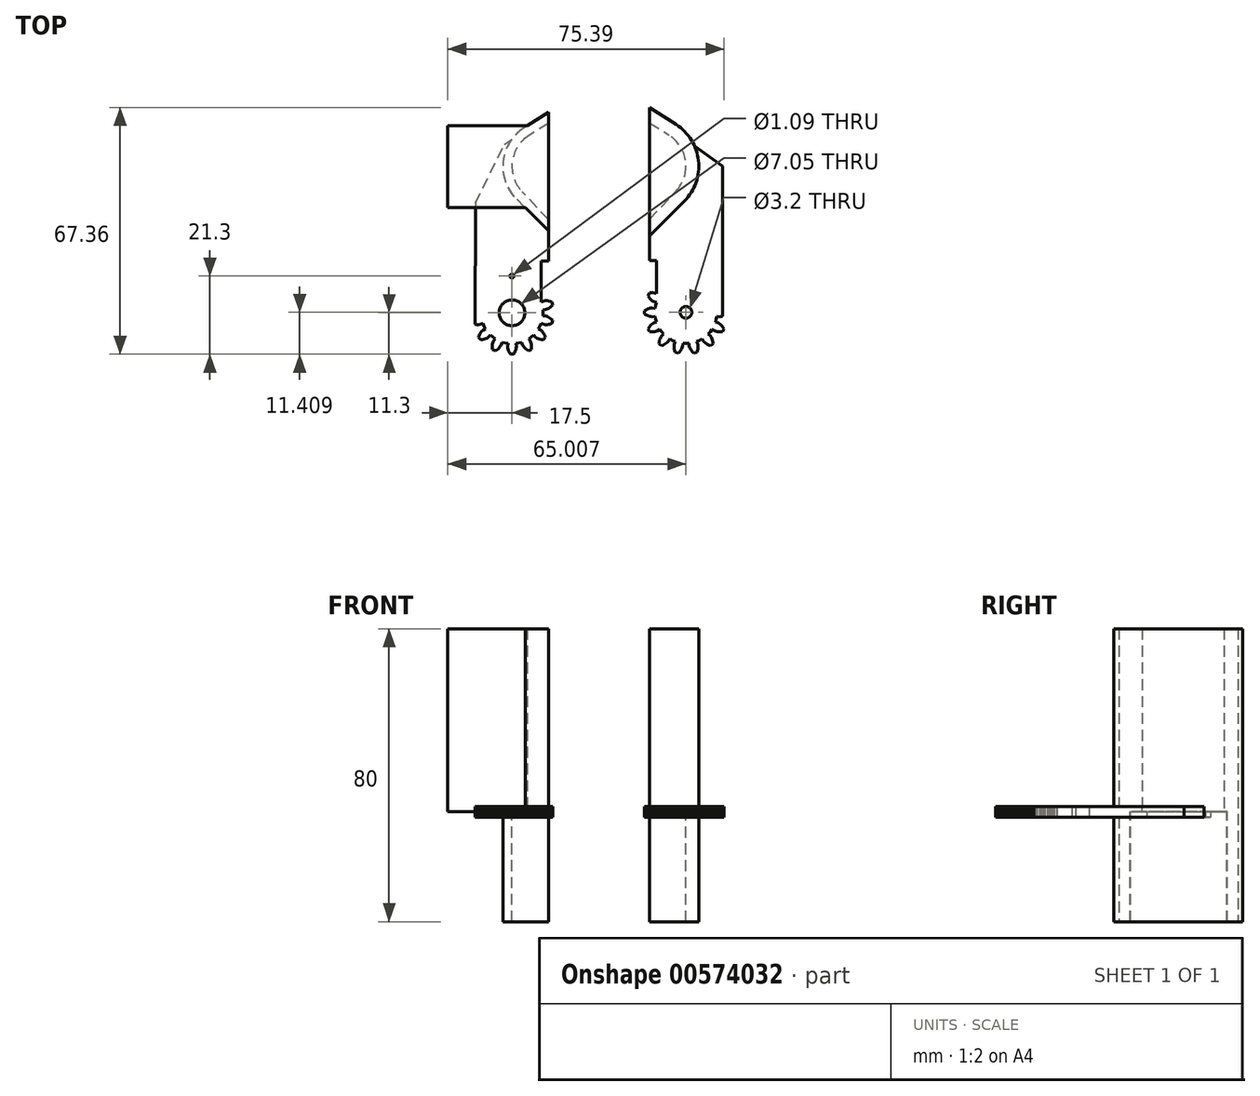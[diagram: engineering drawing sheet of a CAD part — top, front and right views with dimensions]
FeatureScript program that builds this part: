
annotation { "Feature Type Name" : "Feature", "Feature Type Description" : "" }
export const myFeature = defineFeature(function(context is Context, id is Id, definition is map)
    precondition{}
    {
        {
            var Q0;
            Q0=qCreatedBy(makeId("Top.planeOp"),FACE);
            var sketch = newSketch(context, id + "F0", { "sketchPlane" : qUnion([Q0])});
            skLineSegment(sketch, "E0", {"start": v(-11.89, -38.22) * mm, "end": v(-11.08, -38.37) * mm});
            skLineSegment(sketch, "E1", {"start": v(-11.08, -38.37) * mm, "end": v(-11.18, -39.18) * mm});
            skLineSegment(sketch, "E2", {"start": v(-11.18, -39.18) * mm, "end": v(-11.15, -39.59) * mm});
            skLineSegment(sketch, "E3", {"start": v(-11.15, -39.59) * mm, "end": v(-11.05, -40) * mm});
            skLineSegment(sketch, "E4", {"start": v(-11.05, -40) * mm, "end": v(-10.9, -40.42) * mm});
            skLineSegment(sketch, "E5", {"start": v(-10.9, -40.42) * mm, "end": v(-10.7, -40.84) * mm});
            skLineSegment(sketch, "E6", {"start": v(-10.7, -40.84) * mm, "end": v(-10.46, -41.25) * mm});
            skLineSegment(sketch, "E7", {"start": v(-10.46, -41.25) * mm, "end": v(-9.54, -41.25) * mm});
            skLineSegment(sketch, "E8", {"start": v(-9.54, -41.25) * mm, "end": v(-9.3, -40.84) * mm});
            skLineSegment(sketch, "E9", {"start": v(-9.3, -40.84) * mm, "end": v(-9.1, -40.42) * mm});
            skLineSegment(sketch, "E10", {"start": v(-9.1, -40.42) * mm, "end": v(-8.95, -40) * mm});
            skLineSegment(sketch, "E11", {"start": v(-8.95, -40) * mm, "end": v(-8.85, -39.59) * mm});
            skLineSegment(sketch, "E12", {"start": v(-8.85, -39.59) * mm, "end": v(-8.82, -39.18) * mm});
            skLineSegment(sketch, "E13", {"start": v(-8.82, -39.18) * mm, "end": v(-8.92, -38.37) * mm});
            skLineSegment(sketch, "E14", {"start": v(-8.92, -38.37) * mm, "end": v(-8.11, -38.22) * mm});
            skLineSegment(sketch, "E15", {"start": v(-8.11, -38.22) * mm, "end": v(-8.11, -38.22) * mm});
            skLineSegment(sketch, "E16", {"start": v(-8.11, -38.22) * mm, "end": v(-7.32, -38) * mm});
            skLineSegment(sketch, "E17", {"start": v(-7.32, -38) * mm, "end": v(-7.06, -38.78) * mm});
            skLineSegment(sketch, "E18", {"start": v(-7.06, -38.78) * mm, "end": v(-6.86, -39.13) * mm});
            skLineSegment(sketch, "E19", {"start": v(-6.86, -39.13) * mm, "end": v(-6.58, -39.46) * mm});
            skLineSegment(sketch, "E20", {"start": v(-6.58, -39.46) * mm, "end": v(-6.26, -39.77) * mm});
            skLineSegment(sketch, "E21", {"start": v(-6.26, -39.77) * mm, "end": v(-5.9, -40.06) * mm});
            skLineSegment(sketch, "E22", {"start": v(-5.9, -40.06) * mm, "end": v(-5.5, -40.33) * mm});
            skLineSegment(sketch, "E23", {"start": v(-5.5, -40.33) * mm, "end": v(-4.68, -39.94) * mm});
            skLineSegment(sketch, "E24", {"start": v(-4.68, -39.94) * mm, "end": v(-4.65, -39.46) * mm});
            skLineSegment(sketch, "E25", {"start": v(-4.65, -39.46) * mm, "end": v(-4.65, -39) * mm});
            skLineSegment(sketch, "E26", {"start": v(-4.7, -38.55) * mm, "end": v(-4.78, -38.13) * mm});
            skLineSegment(sketch, "E27", {"start": v(-4.78, -38.13) * mm, "end": v(-4.93, -37.75) * mm});
            skLineSegment(sketch, "E28", {"start": v(-4.93, -37.75) * mm, "end": v(-5.38, -37.07) * mm});
            skLineSegment(sketch, "E29", {"start": v(-4.09, -36.04) * mm, "end": v(-3.52, -36.62) * mm});
            skLineSegment(sketch, "E30", {"start": v(-3.18, -36.86) * mm, "end": v(-2.8, -37.04) * mm});
            skLineSegment(sketch, "E31", {"start": v(-2.37, -37.18) * mm, "end": v(-1.92, -37.28) * mm});
            skLineSegment(sketch, "E32", {"start": v(-1.05, -36.2) * mm, "end": v(-1.25, -35.78) * mm});
            skLineSegment(sketch, "E33", {"start": v(-1.25, -35.78) * mm, "end": v(-1.49, -35.4) * mm});
            skLineSegment(sketch, "E34", {"start": v(-2.05, -34.78) * mm, "end": v(-2.75, -34.36) * mm});
            skLineSegment(sketch, "E35", {"start": v(-2.03, -32.87) * mm, "end": v(-1.27, -33.15) * mm});
            skLineSegment(sketch, "E36", {"start": v(-20, -33.15) * mm, "end": v(-19.57, -33.2) * mm});
            skLineSegment(sketch, "E37", {"start": v(-19.57, -33.2) * mm, "end": v(-19.14, -33.22) * mm});
            skLineSegment(sketch, "E38", {"start": v(-19.14, -33.22) * mm, "end": v(-18.73, -33.15) * mm});
            skLineSegment(sketch, "E39", {"start": v(-18.73, -33.15) * mm, "end": v(-17.97, -32.87) * mm});
            skLineSegment(sketch, "E40", {"start": v(-17.97, -32.87) * mm, "end": v(-17.64, -33.63) * mm});
            skLineSegment(sketch, "E41", {"start": v(-17.64, -33.63) * mm, "end": v(-17.65, -33.63) * mm});
            skLineSegment(sketch, "E42", {"start": v(-17.65, -33.63) * mm, "end": v(-17.25, -34.36) * mm});
            skLineSegment(sketch, "E43", {"start": v(-17.25, -34.36) * mm, "end": v(-17.95, -34.78) * mm});
            skLineSegment(sketch, "E44", {"start": v(-17.95, -34.78) * mm, "end": v(-18.25, -35.06) * mm});
            skLineSegment(sketch, "E45", {"start": v(-18.25, -35.06) * mm, "end": v(-18.51, -35.4) * mm});
            skLineSegment(sketch, "E46", {"start": v(-18.51, -35.4) * mm, "end": v(-18.75, -35.78) * mm});
            skLineSegment(sketch, "E47", {"start": v(-18.75, -35.78) * mm, "end": v(-18.95, -36.2) * mm});
            skLineSegment(sketch, "E48", {"start": v(-18.95, -36.2) * mm, "end": v(-19.12, -36.64) * mm});
            skLineSegment(sketch, "E49", {"start": v(-19.12, -36.64) * mm, "end": v(-18.55, -37.36) * mm});
            skLineSegment(sketch, "E50", {"start": v(-18.55, -37.36) * mm, "end": v(-18.08, -37.28) * mm});
            skLineSegment(sketch, "E51", {"start": v(-18.08, -37.28) * mm, "end": v(-17.63, -37.18) * mm});
            skLineSegment(sketch, "E52", {"start": v(-17.63, -37.18) * mm, "end": v(-17.2, -37.04) * mm});
            skLineSegment(sketch, "E53", {"start": v(-17.2, -37.04) * mm, "end": v(-16.82, -36.86) * mm});
            skLineSegment(sketch, "E54", {"start": v(-16.82, -36.86) * mm, "end": v(-16.48, -36.62) * mm});
            skLineSegment(sketch, "E55", {"start": v(-16.48, -36.62) * mm, "end": v(-15.91, -36.04) * mm});
            skLineSegment(sketch, "E56", {"start": v(-15.91, -36.04) * mm, "end": v(-15.3, -36.58) * mm});
            skLineSegment(sketch, "E57", {"start": v(-15.3, -36.58) * mm, "end": v(-15.3, -36.58) * mm});
            skLineSegment(sketch, "E58", {"start": v(-15.3, -36.58) * mm, "end": v(-14.62, -37.07) * mm});
            skLineSegment(sketch, "E59", {"start": v(-14.62, -37.07) * mm, "end": v(-15.07, -37.75) * mm});
            skLineSegment(sketch, "E60", {"start": v(-15.07, -37.75) * mm, "end": v(-15.22, -38.13) * mm});
            skLineSegment(sketch, "E61", {"start": v(-15.22, -38.13) * mm, "end": v(-15.3, -38.55) * mm});
            skLineSegment(sketch, "E62", {"start": v(-15.3, -38.55) * mm, "end": v(-15.35, -39) * mm});
            skLineSegment(sketch, "E63", {"start": v(-15.35, -39) * mm, "end": v(-15.35, -39.46) * mm});
            skLineSegment(sketch, "E64", {"start": v(-15.35, -39.46) * mm, "end": v(-15.32, -39.94) * mm});
            skLineSegment(sketch, "E65", {"start": v(-15.32, -39.94) * mm, "end": v(-14.5, -40.33) * mm});
            skLineSegment(sketch, "E66", {"start": v(-14.5, -40.33) * mm, "end": v(-14.1, -40.06) * mm});
            skLineSegment(sketch, "E67", {"start": v(-14.1, -40.06) * mm, "end": v(-13.74, -39.77) * mm});
            skLineSegment(sketch, "E68", {"start": v(-13.74, -39.77) * mm, "end": v(-13.42, -39.46) * mm});
            skLineSegment(sketch, "E69", {"start": v(-13.42, -39.46) * mm, "end": v(-13.14, -39.13) * mm});
            skLineSegment(sketch, "E70", {"start": v(-13.14, -39.13) * mm, "end": v(-12.94, -38.78) * mm});
            skLineSegment(sketch, "E71", {"start": v(-12.94, -38.78) * mm, "end": v(-12.68, -38) * mm});
            skLineSegment(sketch, "E72", {"start": v(-12.68, -38) * mm, "end": v(-11.89, -38.22) * mm});
            skLineSegment(sketch, "E73", {"start": v(-11.89, -38.22) * mm, "end": v(-11.89, -38.22) * mm});
            skLineSegment(sketch, "E74", {"start": v(-2, -27.02) * mm, "end": v(-2, -15.8) * mm});
            skLineSegment(sketch, "E75", {"start": v(-4.65, -39) * mm, "end": v(-4.7, -38.55) * mm});
            skLineSegment(sketch, "E76", {"start": v(-5.38, -37.07) * mm, "end": v(-4.7, -36.58) * mm});
            skLineSegment(sketch, "E77", {"start": v(-4.7, -36.58) * mm, "end": v(-4.7, -36.58) * mm});
            skLineSegment(sketch, "E78", {"start": v(-4.7, -36.58) * mm, "end": v(-4.09, -36.04) * mm});
            skLineSegment(sketch, "E79", {"start": v(-3.52, -36.62) * mm, "end": v(-3.18, -36.86) * mm});
            skLineSegment(sketch, "E80", {"start": v(-2.8, -37.04) * mm, "end": v(-2.37, -37.18) * mm});
            skLineSegment(sketch, "E81", {"start": v(-1.92, -37.28) * mm, "end": v(-1.45, -37.36) * mm});
            skLineSegment(sketch, "E82", {"start": v(-1.45, -37.36) * mm, "end": v(-0.88, -36.64) * mm});
            skLineSegment(sketch, "E83", {"start": v(-0.88, -36.64) * mm, "end": v(-1.05, -36.2) * mm});
            skLineSegment(sketch, "E84", {"start": v(-1.49, -35.4) * mm, "end": v(-1.75, -35.06) * mm});
            skLineSegment(sketch, "E85", {"start": v(-1.75, -35.06) * mm, "end": v(-2.05, -34.78) * mm});
            skLineSegment(sketch, "E86", {"start": v(-2.75, -34.36) * mm, "end": v(-2.35, -33.63) * mm});
            skLineSegment(sketch, "E87", {"start": v(-2.35, -33.63) * mm, "end": v(-2.36, -33.63) * mm});
            skLineSegment(sketch, "E88", {"start": v(-2.36, -33.63) * mm, "end": v(-2.03, -32.87) * mm});
            skLineSegment(sketch, "E89", {"start": v(-1.27, -33.15) * mm, "end": v(-0.86, -33.22) * mm});
            skLineSegment(sketch, "E90", {"start": v(-0.86, -33.22) * mm, "end": v(-0.43, -33.2) * mm});
            skLineSegment(sketch, "E91", {"start": v(-0.43, -33.2) * mm, "end": v(0, -33.15) * mm});
            skLineSegment(sketch, "E92", {"start": v(0, -33.15) * mm, "end": v(0.46, -33.05) * mm});
            skLineSegment(sketch, "E93", {"start": v(0.46, -33.05) * mm, "end": v(0.92, -32.91) * mm});
            skLineSegment(sketch, "E94", {"start": v(0.92, -32.91) * mm, "end": v(1.12, -32.02) * mm});
            skLineSegment(sketch, "E95", {"start": v(1.12, -32.02) * mm, "end": v(0.77, -31.7) * mm});
            skLineSegment(sketch, "E96", {"start": v(0.77, -31.7) * mm, "end": v(0.4, -31.4) * mm});
            skLineSegment(sketch, "E97", {"start": v(0.4, -31.4) * mm, "end": v(0.03, -31.16) * mm});
            skLineSegment(sketch, "E98", {"start": v(0.03, -31.16) * mm, "end": v(-0.35, -30.97) * mm});
            skLineSegment(sketch, "E99", {"start": v(-0.35, -30.97) * mm, "end": v(-0.74, -30.85) * mm});
            skLineSegment(sketch, "E100", {"start": v(-0.74, -30.85) * mm, "end": v(-1.55, -30.77) * mm});
            skLineSegment(sketch, "E101", {"start": v(-1.55, -30.77) * mm, "end": v(-1.51, -29.95) * mm});
            skLineSegment(sketch, "E102", {"start": v(-1.51, -29.95) * mm, "end": v(-1.51, -29.95) * mm});
            skLineSegment(sketch, "E103", {"start": v(-1.51, -29.95) * mm, "end": v(-1.55, -29.13) * mm});
            skLineSegment(sketch, "E104", {"start": v(-1.55, -29.13) * mm, "end": v(-0.74, -29.05) * mm});
            skLineSegment(sketch, "E105", {"start": v(-0.74, -29.05) * mm, "end": v(-0.35, -28.93) * mm});
            skLineSegment(sketch, "E106", {"start": v(-0.35, -28.93) * mm, "end": v(0.03, -28.74) * mm});
            skLineSegment(sketch, "E107", {"start": v(0.03, -28.74) * mm, "end": v(0.4, -28.5) * mm});
            skLineSegment(sketch, "E108", {"start": v(0.4, -28.5) * mm, "end": v(0.77, -28.2) * mm});
            skLineSegment(sketch, "E109", {"start": v(0.77, -28.2) * mm, "end": v(1.12, -27.88) * mm});
            skLineSegment(sketch, "E110", {"start": v(1.12, -27.88) * mm, "end": v(0.92, -26.99) * mm});
            skLineSegment(sketch, "E111", {"start": v(0.92, -26.99) * mm, "end": v(0.46, -26.85) * mm});
            skLineSegment(sketch, "E112", {"start": v(0.46, -26.85) * mm, "end": v(0, -26.75) * mm});
            skLineSegment(sketch, "E113", {"start": v(0, -26.75) * mm, "end": v(-0.43, -26.69) * mm});
            skLineSegment(sketch, "E114", {"start": v(-0.43, -26.69) * mm, "end": v(-0.86, -26.68) * mm});
            skLineSegment(sketch, "E115", {"start": v(-0.86, -26.68) * mm, "end": v(-1.27, -26.75) * mm});
            skLineSegment(sketch, "E116", {"start": v(-1.27, -26.75) * mm, "end": v(-2, -27.02) * mm});
            skLineSegment(sketch, "E117", {"start": v(45.78, -31.73) * mm, "end": v(45.92, -30.92) * mm});
            skLineSegment(sketch, "E118", {"start": v(45.92, -30.92) * mm, "end": v(46.73, -31.02) * mm});
            skLineSegment(sketch, "E119", {"start": v(46.73, -31.02) * mm, "end": v(47.14, -31) * mm});
            skLineSegment(sketch, "E120", {"start": v(47.14, -31) * mm, "end": v(47.5, -30.9) * mm});
            skLineSegment(sketch, "E121", {"start": v(27.87, -31) * mm, "end": v(28.28, -31.02) * mm});
            skLineSegment(sketch, "E122", {"start": v(29.1, -30.92) * mm, "end": v(29.23, -31.73) * mm});
            skLineSegment(sketch, "E123", {"start": v(28.68, -32.78) * mm, "end": v(28.33, -32.99) * mm});
            skLineSegment(sketch, "E124", {"start": v(27.68, -33.58) * mm, "end": v(27.4, -33.94) * mm});
            skLineSegment(sketch, "E125", {"start": v(28.46, -35.2) * mm, "end": v(28.9, -35.15) * mm});
            skLineSegment(sketch, "E126", {"start": v(28.9, -35.15) * mm, "end": v(29.32, -35.06) * mm});
            skLineSegment(sketch, "E127", {"start": v(29.32, -35.06) * mm, "end": v(29.7, -34.9) * mm});
            skLineSegment(sketch, "E128", {"start": v(29.7, -34.9) * mm, "end": v(30.4, -34.46) * mm});
            skLineSegment(sketch, "E129", {"start": v(30.4, -34.46) * mm, "end": v(30.87, -35.13) * mm});
            skLineSegment(sketch, "E130", {"start": v(30.87, -35.13) * mm, "end": v(30.87, -35.13) * mm});
            skLineSegment(sketch, "E131", {"start": v(31.42, -35.75) * mm, "end": v(30.83, -36.32) * mm});
            skLineSegment(sketch, "E132", {"start": v(30.17, -37.92) * mm, "end": v(30.1, -38.4) * mm});
            skLineSegment(sketch, "E133", {"start": v(30.1, -38.4) * mm, "end": v(30.82, -38.96) * mm});
            skLineSegment(sketch, "E134", {"start": v(30.82, -38.96) * mm, "end": v(31.26, -38.8) * mm});
            skLineSegment(sketch, "E135", {"start": v(31.68, -38.59) * mm, "end": v(32.06, -38.35) * mm});
            skLineSegment(sketch, "E136", {"start": v(32.06, -38.35) * mm, "end": v(32.4, -38.1) * mm});
            skLineSegment(sketch, "E137", {"start": v(32.68, -37.8) * mm, "end": v(33.1, -37.1) * mm});
            skLineSegment(sketch, "E138", {"start": v(33.1, -37.1) * mm, "end": v(33.83, -37.49) * mm});
            skLineSegment(sketch, "E139", {"start": v(33.83, -37.49) * mm, "end": v(33.83, -37.49) * mm});
            skLineSegment(sketch, "E140", {"start": v(34.59, -37.8) * mm, "end": v(34.3, -38.58) * mm});
            skLineSegment(sketch, "E141", {"start": v(34.4, -40.3) * mm, "end": v(34.55, -40.76) * mm});
            skLineSegment(sketch, "E142", {"start": v(35.44, -40.96) * mm, "end": v(35.76, -40.61) * mm});
            skLineSegment(sketch, "E143", {"start": v(36.05, -40.25) * mm, "end": v(36.3, -39.88) * mm});
            skLineSegment(sketch, "E144", {"start": v(36.68, -38.29) * mm, "end": v(37.5, -38.33) * mm});
            skLineSegment(sketch, "E145", {"start": v(37.5, -38.33) * mm, "end": v(37.5, -38.33) * mm});
            skLineSegment(sketch, "E146", {"start": v(37.5, -38.33) * mm, "end": v(38.33, -38.29) * mm});
            skLineSegment(sketch, "E147", {"start": v(38.33, -38.29) * mm, "end": v(38.41, -39.1) * mm});
            skLineSegment(sketch, "E148", {"start": v(38.41, -39.1) * mm, "end": v(38.53, -39.5) * mm});
            skLineSegment(sketch, "E149", {"start": v(38.53, -39.5) * mm, "end": v(38.72, -39.88) * mm});
            skLineSegment(sketch, "E150", {"start": v(38.72, -39.88) * mm, "end": v(38.96, -40.25) * mm});
            skLineSegment(sketch, "E151", {"start": v(38.96, -40.25) * mm, "end": v(39.25, -40.61) * mm});
            skLineSegment(sketch, "E152", {"start": v(39.25, -40.61) * mm, "end": v(39.58, -40.96) * mm});
            skLineSegment(sketch, "E153", {"start": v(39.58, -40.96) * mm, "end": v(40.47, -40.76) * mm});
            skLineSegment(sketch, "E154", {"start": v(40.47, -40.76) * mm, "end": v(40.61, -40.3) * mm});
            skLineSegment(sketch, "E155", {"start": v(40.61, -40.3) * mm, "end": v(40.71, -39.85) * mm});
            skLineSegment(sketch, "E156", {"start": v(40.71, -39.85) * mm, "end": v(40.77, -39.4) * mm});
            skLineSegment(sketch, "E157", {"start": v(40.77, -39.4) * mm, "end": v(40.77, -38.98) * mm});
            skLineSegment(sketch, "E158", {"start": v(40.77, -38.98) * mm, "end": v(40.7, -38.58) * mm});
            skLineSegment(sketch, "E159", {"start": v(40.7, -38.58) * mm, "end": v(40.43, -37.8) * mm});
            skLineSegment(sketch, "E160", {"start": v(40.43, -37.8) * mm, "end": v(41.19, -37.49) * mm});
            skLineSegment(sketch, "E161", {"start": v(41.19, -37.49) * mm, "end": v(41.19, -37.49) * mm});
            skLineSegment(sketch, "E162", {"start": v(41.19, -37.49) * mm, "end": v(41.91, -37.1) * mm});
            skLineSegment(sketch, "E163", {"start": v(41.91, -37.1) * mm, "end": v(42.34, -37.8) * mm});
            skLineSegment(sketch, "E164", {"start": v(42.34, -37.8) * mm, "end": v(42.62, -38.1) * mm});
            skLineSegment(sketch, "E165", {"start": v(42.62, -38.1) * mm, "end": v(42.95, -38.35) * mm});
            skLineSegment(sketch, "E166", {"start": v(42.95, -38.35) * mm, "end": v(43.33, -38.59) * mm});
            skLineSegment(sketch, "E167", {"start": v(43.33, -38.59) * mm, "end": v(43.75, -38.8) * mm});
            skLineSegment(sketch, "E168", {"start": v(43.75, -38.8) * mm, "end": v(44.2, -38.96) * mm});
            skLineSegment(sketch, "E169", {"start": v(44.2, -38.96) * mm, "end": v(44.91, -38.4) * mm});
            skLineSegment(sketch, "E170", {"start": v(44.91, -38.4) * mm, "end": v(44.84, -37.92) * mm});
            skLineSegment(sketch, "E171", {"start": v(44.84, -37.92) * mm, "end": v(44.74, -37.47) * mm});
            skLineSegment(sketch, "E172", {"start": v(44.74, -37.47) * mm, "end": v(44.6, -37.05) * mm});
            skLineSegment(sketch, "E173", {"start": v(44.6, -37.05) * mm, "end": v(44.41, -36.66) * mm});
            skLineSegment(sketch, "E174", {"start": v(44.41, -36.66) * mm, "end": v(44.18, -36.32) * mm});
            skLineSegment(sketch, "E175", {"start": v(44.18, -36.32) * mm, "end": v(43.6, -35.75) * mm});
            skLineSegment(sketch, "E176", {"start": v(43.6, -35.75) * mm, "end": v(44.14, -35.13) * mm});
            skLineSegment(sketch, "E177", {"start": v(44.14, -35.13) * mm, "end": v(44.14, -35.13) * mm});
            skLineSegment(sketch, "E178", {"start": v(44.14, -35.13) * mm, "end": v(44.62, -34.46) * mm});
            skLineSegment(sketch, "E179", {"start": v(44.62, -34.46) * mm, "end": v(45.3, -34.9) * mm});
            skLineSegment(sketch, "E180", {"start": v(45.3, -34.9) * mm, "end": v(45.69, -35.06) * mm});
            skLineSegment(sketch, "E181", {"start": v(45.69, -35.06) * mm, "end": v(46.1, -35.15) * mm});
            skLineSegment(sketch, "E182", {"start": v(46.1, -35.15) * mm, "end": v(46.55, -35.2) * mm});
            skLineSegment(sketch, "E183", {"start": v(46.55, -35.2) * mm, "end": v(47.01, -35.2) * mm});
            skLineSegment(sketch, "E184", {"start": v(47.01, -35.2) * mm, "end": v(47.5, -35.16) * mm});
            skLineSegment(sketch, "E185", {"start": v(47.5, -35.16) * mm, "end": v(47.9, -34.33) * mm});
            skLineSegment(sketch, "E186", {"start": v(47.9, -34.33) * mm, "end": v(47.62, -33.94) * mm});
            skLineSegment(sketch, "E187", {"start": v(47.62, -33.94) * mm, "end": v(47.33, -33.58) * mm});
            skLineSegment(sketch, "E188", {"start": v(47.33, -33.58) * mm, "end": v(47.02, -33.26) * mm});
            skLineSegment(sketch, "E189", {"start": v(47.02, -33.26) * mm, "end": v(46.69, -32.99) * mm});
            skLineSegment(sketch, "E190", {"start": v(46.69, -32.99) * mm, "end": v(46.33, -32.78) * mm});
            skLineSegment(sketch, "E191", {"start": v(46.33, -32.78) * mm, "end": v(45.56, -32.52) * mm});
            skLineSegment(sketch, "E192", {"start": v(45.56, -32.52) * mm, "end": v(45.78, -31.73) * mm});
            skLineSegment(sketch, "E193", {"start": v(45.78, -31.73) * mm, "end": v(45.78, -31.73) * mm});
            skLineSegment(sketch, "E194", {"start": v(29.5, -24.7) * mm, "end": v(29.5, -15.7) * mm});
            skLineSegment(sketch, "E195", {"start": v(47.5, -30.9) * mm, "end": v(47.5, 10.1) * mm});
            skLineSegment(sketch, "E196", {"start": v(29.5, -24.7) * mm, "end": v(29.32, -24.62) * mm});
            skLineSegment(sketch, "E197", {"start": v(29.32, -24.62) * mm, "end": v(28.9, -24.53) * mm});
            skLineSegment(sketch, "E198", {"start": v(28.9, -24.53) * mm, "end": v(28.46, -24.5) * mm});
            skLineSegment(sketch, "E199", {"start": v(28.46, -24.5) * mm, "end": v(28, -24.49) * mm});
            skLineSegment(sketch, "E200", {"start": v(28, -24.49) * mm, "end": v(27.52, -24.53) * mm});
            skLineSegment(sketch, "E201", {"start": v(27.52, -24.53) * mm, "end": v(27.12, -25.35) * mm});
            skLineSegment(sketch, "E202", {"start": v(27.12, -25.35) * mm, "end": v(27.4, -25.75) * mm});
            skLineSegment(sketch, "E203", {"start": v(27.4, -25.75) * mm, "end": v(27.68, -26.1) * mm});
            skLineSegment(sketch, "E204", {"start": v(27.68, -26.1) * mm, "end": v(28, -26.43) * mm});
            skLineSegment(sketch, "E205", {"start": v(28, -26.43) * mm, "end": v(28.33, -26.7) * mm});
            skLineSegment(sketch, "E206", {"start": v(28.33, -26.7) * mm, "end": v(28.68, -26.9) * mm});
            skLineSegment(sketch, "E207", {"start": v(28.68, -26.9) * mm, "end": v(29.46, -27.16) * mm});
            skLineSegment(sketch, "E208", {"start": v(29.46, -27.16) * mm, "end": v(29.23, -27.95) * mm});
            skLineSegment(sketch, "E209", {"start": v(29.23, -27.95) * mm, "end": v(29.23, -27.95) * mm});
            skLineSegment(sketch, "E210", {"start": v(29.23, -27.95) * mm, "end": v(29.1, -28.77) * mm});
            skLineSegment(sketch, "E211", {"start": v(29.1, -28.77) * mm, "end": v(28.28, -28.66) * mm});
            skLineSegment(sketch, "E212", {"start": v(28.28, -28.66) * mm, "end": v(27.87, -28.7) * mm});
            skLineSegment(sketch, "E213", {"start": v(27.87, -28.7) * mm, "end": v(27.45, -28.8) * mm});
            skLineSegment(sketch, "E214", {"start": v(27.45, -28.8) * mm, "end": v(27.04, -28.94) * mm});
            skLineSegment(sketch, "E215", {"start": v(27.04, -28.94) * mm, "end": v(26.62, -29.14) * mm});
            skLineSegment(sketch, "E216", {"start": v(26.62, -29.14) * mm, "end": v(26.2, -29.38) * mm});
            skLineSegment(sketch, "E217", {"start": v(26.2, -30.3) * mm, "end": v(26.62, -30.54) * mm});
            skLineSegment(sketch, "E218", {"start": v(26.62, -30.54) * mm, "end": v(27.04, -30.74) * mm});
            skLineSegment(sketch, "E219", {"start": v(27.04, -30.74) * mm, "end": v(27.45, -30.9) * mm});
            skLineSegment(sketch, "E220", {"start": v(27.45, -30.9) * mm, "end": v(27.87, -31) * mm});
            skLineSegment(sketch, "E221", {"start": v(28.28, -31.02) * mm, "end": v(29.1, -30.92) * mm});
            skLineSegment(sketch, "E222", {"start": v(29.23, -31.73) * mm, "end": v(29.23, -31.73) * mm});
            skLineSegment(sketch, "E223", {"start": v(29.23, -31.73) * mm, "end": v(29.46, -32.52) * mm});
            skLineSegment(sketch, "E224", {"start": v(29.46, -32.52) * mm, "end": v(28.68, -32.78) * mm});
            skLineSegment(sketch, "E225", {"start": v(28.33, -32.99) * mm, "end": v(28, -33.26) * mm});
            skLineSegment(sketch, "E226", {"start": v(28, -33.26) * mm, "end": v(27.68, -33.58) * mm});
            skLineSegment(sketch, "E227", {"start": v(27.4, -33.94) * mm, "end": v(27.12, -34.33) * mm});
            skLineSegment(sketch, "E228", {"start": v(27.12, -34.33) * mm, "end": v(27.52, -35.16) * mm});
            skLineSegment(sketch, "E229", {"start": v(27.52, -35.16) * mm, "end": v(28, -35.2) * mm});
            skLineSegment(sketch, "E230", {"start": v(28, -35.2) * mm, "end": v(28.46, -35.2) * mm});
            skLineSegment(sketch, "E231", {"start": v(30.87, -35.13) * mm, "end": v(31.42, -35.75) * mm});
            skLineSegment(sketch, "E232", {"start": v(30.83, -36.32) * mm, "end": v(30.6, -36.66) * mm});
            skLineSegment(sketch, "E233", {"start": v(30.6, -36.66) * mm, "end": v(30.42, -37.05) * mm});
            skLineSegment(sketch, "E234", {"start": v(30.42, -37.05) * mm, "end": v(30.28, -37.47) * mm});
            skLineSegment(sketch, "E235", {"start": v(30.28, -37.47) * mm, "end": v(30.17, -37.92) * mm});
            skLineSegment(sketch, "E236", {"start": v(31.26, -38.8) * mm, "end": v(31.68, -38.59) * mm});
            skLineSegment(sketch, "E237", {"start": v(32.4, -38.1) * mm, "end": v(32.68, -37.8) * mm});
            skLineSegment(sketch, "E238", {"start": v(33.83, -37.49) * mm, "end": v(34.59, -37.8) * mm});
            skLineSegment(sketch, "E239", {"start": v(34.3, -38.58) * mm, "end": v(34.24, -38.98) * mm});
            skLineSegment(sketch, "E240", {"start": v(34.24, -38.98) * mm, "end": v(34.25, -39.4) * mm});
            skLineSegment(sketch, "E241", {"start": v(34.25, -39.4) * mm, "end": v(34.3, -39.85) * mm});
            skLineSegment(sketch, "E242", {"start": v(34.3, -39.85) * mm, "end": v(34.4, -40.3) * mm});
            skLineSegment(sketch, "E243", {"start": v(34.55, -40.76) * mm, "end": v(35.44, -40.96) * mm});
            skLineSegment(sketch, "E244", {"start": v(35.76, -40.61) * mm, "end": v(36.05, -40.25) * mm});
            skLineSegment(sketch, "E245", {"start": v(36.3, -39.88) * mm, "end": v(36.48, -39.5) * mm});
            skLineSegment(sketch, "E246", {"start": v(36.48, -39.5) * mm, "end": v(36.6, -39.1) * mm});
            skLineSegment(sketch, "E247", {"start": v(36.6, -39.1) * mm, "end": v(36.68, -38.29) * mm});
            skLineSegment(sketch, "E248", {"start": v(26.2, -29.38) * mm, "end": v(26.2, -30.3) * mm});
            skCircle(sketch, "E249", {"center": v(37.5, -29.84) * mm, "radius": 1.6 * mm});
            skCircle(sketch, "E250", {"center": v(-10, -29.95) * mm, "radius": 3.52 * mm});
            skCircle(sketch, "E251", {"center": v(-10, -19.95) * mm, "radius": 0.55 * mm});
            skLineSegment(sketch, "E252", {"start": v(97.08, -42.45) * mm, "end": v(97.9, -42.59) * mm});
            skLineSegment(sketch, "E253", {"start": v(97.9, -42.59) * mm, "end": v(97.8, -43.4) * mm});
            skLineSegment(sketch, "E254", {"start": v(97.8, -43.4) * mm, "end": v(97.82, -43.8) * mm});
            skLineSegment(sketch, "E255", {"start": v(97.82, -43.8) * mm, "end": v(97.92, -44.23) * mm});
            skLineSegment(sketch, "E256", {"start": v(97.92, -44.23) * mm, "end": v(98.07, -44.64) * mm});
            skLineSegment(sketch, "E257", {"start": v(98.07, -44.64) * mm, "end": v(98.27, -45.06) * mm});
            skLineSegment(sketch, "E258", {"start": v(98.27, -45.06) * mm, "end": v(98.51, -45.48) * mm});
            skLineSegment(sketch, "E259", {"start": v(98.51, -45.48) * mm, "end": v(99.43, -45.48) * mm});
            skLineSegment(sketch, "E260", {"start": v(99.43, -45.48) * mm, "end": v(99.67, -45.06) * mm});
            skLineSegment(sketch, "E261", {"start": v(99.67, -45.06) * mm, "end": v(99.87, -44.64) * mm});
            skLineSegment(sketch, "E262", {"start": v(99.87, -44.64) * mm, "end": v(100.02, -44.23) * mm});
            skLineSegment(sketch, "E263", {"start": v(100.02, -44.23) * mm, "end": v(100.12, -43.8) * mm});
            skLineSegment(sketch, "E264", {"start": v(100.12, -43.8) * mm, "end": v(100.15, -43.4) * mm});
            skLineSegment(sketch, "E265", {"start": v(100.15, -43.4) * mm, "end": v(100.05, -42.59) * mm});
            skLineSegment(sketch, "E266", {"start": v(100.05, -42.59) * mm, "end": v(100.86, -42.45) * mm});
            skLineSegment(sketch, "E267", {"start": v(100.86, -42.45) * mm, "end": v(100.86, -42.45) * mm});
            skLineSegment(sketch, "E268", {"start": v(100.86, -42.45) * mm, "end": v(101.65, -42.22) * mm});
            skLineSegment(sketch, "E269", {"start": v(101.65, -42.22) * mm, "end": v(101.91, -43) * mm});
            skLineSegment(sketch, "E270", {"start": v(101.91, -43) * mm, "end": v(102.12, -43.35) * mm});
            skLineSegment(sketch, "E271", {"start": v(102.12, -43.35) * mm, "end": v(102.39, -43.68) * mm});
            skLineSegment(sketch, "E272", {"start": v(102.39, -43.68) * mm, "end": v(102.7, -44) * mm});
            skLineSegment(sketch, "E273", {"start": v(102.7, -44) * mm, "end": v(103.07, -44.29) * mm});
            skLineSegment(sketch, "E274", {"start": v(103.07, -44.29) * mm, "end": v(103.46, -44.56) * mm});
            skLineSegment(sketch, "E275", {"start": v(103.46, -44.56) * mm, "end": v(104.29, -44.16) * mm});
            skLineSegment(sketch, "E276", {"start": v(104.29, -44.16) * mm, "end": v(104.32, -43.68) * mm});
            skLineSegment(sketch, "E277", {"start": v(104.32, -43.68) * mm, "end": v(104.32, -43.22) * mm});
            skLineSegment(sketch, "E278", {"start": v(104.28, -42.77) * mm, "end": v(104.19, -42.36) * mm});
            skLineSegment(sketch, "E279", {"start": v(104.19, -42.36) * mm, "end": v(104.04, -41.97) * mm});
            skLineSegment(sketch, "E280", {"start": v(104.04, -41.97) * mm, "end": v(103.6, -41.29) * mm});
            skLineSegment(sketch, "E281", {"start": v(104.88, -40.26) * mm, "end": v(105.45, -40.85) * mm});
            skLineSegment(sketch, "E282", {"start": v(105.79, -41.08) * mm, "end": v(106.18, -41.26) * mm});
            skLineSegment(sketch, "E283", {"start": v(106.6, -41.4) * mm, "end": v(107.05, -41.5) * mm});
            skLineSegment(sketch, "E284", {"start": v(107.92, -40.42) * mm, "end": v(107.72, -40) * mm});
            skLineSegment(sketch, "E285", {"start": v(107.72, -40) * mm, "end": v(107.48, -39.62) * mm});
            skLineSegment(sketch, "E286", {"start": v(106.92, -39) * mm, "end": v(106.22, -38.58) * mm});
            skLineSegment(sketch, "E287", {"start": v(106.94, -37.1) * mm, "end": v(107.7, -37.38) * mm});
            skLineSegment(sketch, "E288", {"start": v(88.96, -37.38) * mm, "end": v(89.4, -37.43) * mm});
            skLineSegment(sketch, "E289", {"start": v(89.4, -37.43) * mm, "end": v(89.83, -37.44) * mm});
            skLineSegment(sketch, "E290", {"start": v(89.83, -37.44) * mm, "end": v(90.24, -37.38) * mm});
            skLineSegment(sketch, "E291", {"start": v(90.24, -37.38) * mm, "end": v(91, -37.1) * mm});
            skLineSegment(sketch, "E292", {"start": v(91, -37.1) * mm, "end": v(91.33, -37.85) * mm});
            skLineSegment(sketch, "E293", {"start": v(91.33, -37.85) * mm, "end": v(91.33, -37.85) * mm});
            skLineSegment(sketch, "E294", {"start": v(91.33, -37.85) * mm, "end": v(91.72, -38.58) * mm});
            skLineSegment(sketch, "E295", {"start": v(91.72, -38.58) * mm, "end": v(91.02, -39) * mm});
            skLineSegment(sketch, "E296", {"start": v(91.02, -39) * mm, "end": v(90.72, -39.28) * mm});
            skLineSegment(sketch, "E297", {"start": v(90.72, -39.28) * mm, "end": v(90.46, -39.62) * mm});
            skLineSegment(sketch, "E298", {"start": v(90.46, -39.62) * mm, "end": v(90.23, -40) * mm});
            skLineSegment(sketch, "E299", {"start": v(90.23, -40) * mm, "end": v(90.02, -40.42) * mm});
            skLineSegment(sketch, "E300", {"start": v(90.02, -40.42) * mm, "end": v(89.85, -40.86) * mm});
            skLineSegment(sketch, "E301", {"start": v(89.85, -40.86) * mm, "end": v(90.42, -41.58) * mm});
            skLineSegment(sketch, "E302", {"start": v(90.42, -41.58) * mm, "end": v(90.9, -41.5) * mm});
            skLineSegment(sketch, "E303", {"start": v(90.9, -41.5) * mm, "end": v(91.34, -41.4) * mm});
            skLineSegment(sketch, "E304", {"start": v(91.34, -41.4) * mm, "end": v(91.77, -41.26) * mm});
            skLineSegment(sketch, "E305", {"start": v(91.77, -41.26) * mm, "end": v(92.15, -41.08) * mm});
            skLineSegment(sketch, "E306", {"start": v(92.15, -41.08) * mm, "end": v(92.5, -40.85) * mm});
            skLineSegment(sketch, "E307", {"start": v(92.5, -40.85) * mm, "end": v(93.06, -40.26) * mm});
            skLineSegment(sketch, "E308", {"start": v(93.06, -40.26) * mm, "end": v(93.68, -40.8) * mm});
            skLineSegment(sketch, "E309", {"start": v(93.68, -40.8) * mm, "end": v(93.68, -40.8) * mm});
            skLineSegment(sketch, "E310", {"start": v(93.68, -40.8) * mm, "end": v(94.35, -41.29) * mm});
            skLineSegment(sketch, "E311", {"start": v(94.35, -41.29) * mm, "end": v(93.9, -41.97) * mm});
            skLineSegment(sketch, "E312", {"start": v(93.9, -41.97) * mm, "end": v(93.75, -42.36) * mm});
            skLineSegment(sketch, "E313", {"start": v(93.75, -42.36) * mm, "end": v(93.66, -42.77) * mm});
            skLineSegment(sketch, "E314", {"start": v(93.66, -42.77) * mm, "end": v(93.62, -43.22) * mm});
            skLineSegment(sketch, "E315", {"start": v(93.62, -43.22) * mm, "end": v(93.62, -43.68) * mm});
            skLineSegment(sketch, "E316", {"start": v(93.62, -43.68) * mm, "end": v(93.65, -44.16) * mm});
            skLineSegment(sketch, "E317", {"start": v(93.65, -44.16) * mm, "end": v(94.48, -44.56) * mm});
            skLineSegment(sketch, "E318", {"start": v(94.48, -44.56) * mm, "end": v(94.87, -44.29) * mm});
            skLineSegment(sketch, "E319", {"start": v(94.87, -44.29) * mm, "end": v(95.24, -44) * mm});
            skLineSegment(sketch, "E320", {"start": v(95.24, -44) * mm, "end": v(95.55, -43.68) * mm});
            skLineSegment(sketch, "E321", {"start": v(95.55, -43.68) * mm, "end": v(95.83, -43.35) * mm});
            skLineSegment(sketch, "E322", {"start": v(95.83, -43.35) * mm, "end": v(96.03, -43) * mm});
            skLineSegment(sketch, "E323", {"start": v(96.03, -43) * mm, "end": v(96.29, -42.22) * mm});
            skLineSegment(sketch, "E324", {"start": v(96.29, -42.22) * mm, "end": v(97.08, -42.45) * mm});
            skLineSegment(sketch, "E325", {"start": v(97.08, -42.45) * mm, "end": v(97.08, -42.45) * mm});
            skLineSegment(sketch, "E326", {"start": v(98.97, -2.1) * mm, "end": v(98.97, 13.76) * mm});
            skArc(sketch, "E327", {"start": v(98.97, -2.1) * mm, "mid": v(99.35, -4.02) * mm, "end": v(100.44, -5.64) * mm});
            skLineSegment(sketch, "E328", {"start": v(106.97, -31.24) * mm, "end": v(106.97, -14.24) * mm});
            skArc(sketch, "E329", {"start": v(106.97, -14.24) * mm, "mid": v(106.6, -12.33) * mm, "end": v(105.5, -10.7) * mm});
            skLineSegment(sketch, "E330", {"start": v(108.97, 25.83) * mm, "end": v(108.97, 40.83) * mm});
            skLineSegment(sketch, "E331", {"start": v(108.97, 40.83) * mm, "end": v(106.04, 40.83) * mm});
            skArc(sketch, "E332", {"start": v(106.04, 40.83) * mm, "mid": v(104.13, 40.45) * mm, "end": v(102.5, 39.36) * mm});
            skLineSegment(sketch, "E333", {"start": v(88.96, -37.38) * mm, "end": v(88.97, 23.76) * mm});
            skLineSegment(sketch, "E334", {"start": v(102.5, 39.36) * mm, "end": v(90.43, 27.3) * mm});
            skArc(sketch, "E335", {"start": v(90.43, 27.3) * mm, "mid": v(89.35, 25.67) * mm, "end": v(88.97, 23.76) * mm});
            skLineSegment(sketch, "E336", {"start": v(108.97, 25.83) * mm, "end": v(100.44, 17.3) * mm});
            skArc(sketch, "E337", {"start": v(100.44, 17.3) * mm, "mid": v(99.35, 15.67) * mm, "end": v(98.97, 13.76) * mm});
            skLineSegment(sketch, "E338", {"start": v(100.44, -5.64) * mm, "end": v(105.5, -10.7) * mm});
            skLineSegment(sketch, "E339", {"start": v(104.32, -43.22) * mm, "end": v(104.28, -42.77) * mm});
            skLineSegment(sketch, "E340", {"start": v(103.6, -41.29) * mm, "end": v(104.26, -40.8) * mm});
            skLineSegment(sketch, "E341", {"start": v(104.26, -40.8) * mm, "end": v(104.26, -40.8) * mm});
            skLineSegment(sketch, "E342", {"start": v(104.26, -40.8) * mm, "end": v(104.88, -40.26) * mm});
            skLineSegment(sketch, "E343", {"start": v(105.45, -40.85) * mm, "end": v(105.79, -41.08) * mm});
            skLineSegment(sketch, "E344", {"start": v(106.18, -41.26) * mm, "end": v(106.6, -41.4) * mm});
            skLineSegment(sketch, "E345", {"start": v(107.05, -41.5) * mm, "end": v(107.52, -41.58) * mm});
            skLineSegment(sketch, "E346", {"start": v(107.52, -41.58) * mm, "end": v(108.1, -40.86) * mm});
            skLineSegment(sketch, "E347", {"start": v(108.1, -40.86) * mm, "end": v(107.92, -40.42) * mm});
            skLineSegment(sketch, "E348", {"start": v(107.48, -39.62) * mm, "end": v(107.22, -39.28) * mm});
            skLineSegment(sketch, "E349", {"start": v(107.22, -39.28) * mm, "end": v(106.92, -39) * mm});
            skLineSegment(sketch, "E350", {"start": v(106.22, -38.58) * mm, "end": v(106.62, -37.85) * mm});
            skLineSegment(sketch, "E351", {"start": v(106.62, -37.85) * mm, "end": v(106.62, -37.85) * mm});
            skLineSegment(sketch, "E352", {"start": v(106.62, -37.85) * mm, "end": v(106.94, -37.1) * mm});
            skLineSegment(sketch, "E353", {"start": v(107.7, -37.38) * mm, "end": v(108.1, -37.44) * mm});
            skLineSegment(sketch, "E354", {"start": v(108.1, -37.44) * mm, "end": v(108.54, -37.43) * mm});
            skLineSegment(sketch, "E355", {"start": v(108.54, -37.43) * mm, "end": v(108.98, -37.38) * mm});
            skLineSegment(sketch, "E356", {"start": v(108.98, -37.38) * mm, "end": v(109.43, -37.28) * mm});
            skLineSegment(sketch, "E357", {"start": v(109.43, -37.28) * mm, "end": v(109.9, -37.13) * mm});
            skLineSegment(sketch, "E358", {"start": v(109.9, -37.13) * mm, "end": v(110.1, -36.24) * mm});
            skLineSegment(sketch, "E359", {"start": v(110.1, -36.24) * mm, "end": v(109.74, -35.92) * mm});
            skLineSegment(sketch, "E360", {"start": v(109.74, -35.92) * mm, "end": v(109.38, -35.63) * mm});
            skLineSegment(sketch, "E361", {"start": v(109.38, -35.63) * mm, "end": v(109, -35.39) * mm});
            skLineSegment(sketch, "E362", {"start": v(109, -35.39) * mm, "end": v(108.62, -35.2) * mm});
            skLineSegment(sketch, "E363", {"start": v(108.62, -35.2) * mm, "end": v(108.23, -35.08) * mm});
            skLineSegment(sketch, "E364", {"start": v(108.23, -35.08) * mm, "end": v(107.42, -35) * mm});
            skLineSegment(sketch, "E365", {"start": v(107.42, -35) * mm, "end": v(107.46, -34.17) * mm});
            skLineSegment(sketch, "E366", {"start": v(107.46, -34.17) * mm, "end": v(107.46, -34.17) * mm});
            skLineSegment(sketch, "E367", {"start": v(107.46, -34.17) * mm, "end": v(107.42, -33.35) * mm});
            skLineSegment(sketch, "E368", {"start": v(107.42, -33.35) * mm, "end": v(108.23, -33.27) * mm});
            skLineSegment(sketch, "E369", {"start": v(108.23, -33.27) * mm, "end": v(108.62, -33.15) * mm});
            skLineSegment(sketch, "E370", {"start": v(108.62, -33.15) * mm, "end": v(109, -32.96) * mm});
            skLineSegment(sketch, "E371", {"start": v(109, -32.96) * mm, "end": v(109.38, -32.72) * mm});
            skLineSegment(sketch, "E372", {"start": v(109.38, -32.72) * mm, "end": v(109.74, -32.43) * mm});
            skLineSegment(sketch, "E373", {"start": v(109.74, -32.43) * mm, "end": v(110.1, -32.1) * mm});
            skLineSegment(sketch, "E374", {"start": v(110.1, -32.1) * mm, "end": v(109.9, -31.21) * mm});
            skLineSegment(sketch, "E375", {"start": v(109.9, -31.21) * mm, "end": v(109.43, -31.07) * mm});
            skLineSegment(sketch, "E376", {"start": v(109.43, -31.07) * mm, "end": v(108.98, -30.97) * mm});
            skLineSegment(sketch, "E377", {"start": v(108.98, -30.97) * mm, "end": v(108.54, -30.91) * mm});
            skLineSegment(sketch, "E378", {"start": v(108.54, -30.91) * mm, "end": v(108.1, -30.9) * mm});
            skLineSegment(sketch, "E379", {"start": v(108.1, -30.9) * mm, "end": v(107.7, -30.97) * mm});
            skLineSegment(sketch, "E380", {"start": v(107.7, -30.97) * mm, "end": v(106.97, -31.24) * mm});
            skLineSegment(sketch, "E381", {"start": v(150.9, -35.72) * mm, "end": v(151.04, -34.9) * mm});
            skLineSegment(sketch, "E382", {"start": v(151.04, -34.9) * mm, "end": v(151.85, -35) * mm});
            skLineSegment(sketch, "E383", {"start": v(151.85, -35) * mm, "end": v(152.25, -34.98) * mm});
            skLineSegment(sketch, "E384", {"start": v(152.25, -34.98) * mm, "end": v(152.62, -34.89) * mm});
            skLineSegment(sketch, "E385", {"start": v(132.98, -34.98) * mm, "end": v(133.4, -35) * mm});
            skLineSegment(sketch, "E386", {"start": v(134.2, -34.9) * mm, "end": v(134.35, -35.72) * mm});
            skLineSegment(sketch, "E387", {"start": v(133.8, -36.77) * mm, "end": v(133.44, -36.97) * mm});
            skLineSegment(sketch, "E388", {"start": v(132.8, -37.56) * mm, "end": v(132.5, -37.92) * mm});
            skLineSegment(sketch, "E389", {"start": v(133.57, -39.18) * mm, "end": v(134.02, -39.13) * mm});
            skLineSegment(sketch, "E390", {"start": v(134.02, -39.13) * mm, "end": v(134.44, -39.04) * mm});
            skLineSegment(sketch, "E391", {"start": v(134.44, -39.04) * mm, "end": v(134.82, -38.9) * mm});
            skLineSegment(sketch, "E392", {"start": v(134.82, -38.9) * mm, "end": v(135.5, -38.45) * mm});
            skLineSegment(sketch, "E393", {"start": v(135.5, -38.45) * mm, "end": v(135.98, -39.12) * mm});
            skLineSegment(sketch, "E394", {"start": v(135.98, -39.12) * mm, "end": v(135.98, -39.12) * mm});
            skLineSegment(sketch, "E395", {"start": v(136.53, -39.74) * mm, "end": v(135.94, -40.3) * mm});
            skLineSegment(sketch, "E396", {"start": v(135.28, -41.9) * mm, "end": v(135.21, -42.38) * mm});
            skLineSegment(sketch, "E397", {"start": v(135.21, -42.38) * mm, "end": v(135.93, -42.95) * mm});
            skLineSegment(sketch, "E398", {"start": v(135.93, -42.95) * mm, "end": v(136.37, -42.78) * mm});
            skLineSegment(sketch, "E399", {"start": v(136.8, -42.57) * mm, "end": v(137.17, -42.34) * mm});
            skLineSegment(sketch, "E400", {"start": v(137.17, -42.34) * mm, "end": v(137.5, -42.08) * mm});
            skLineSegment(sketch, "E401", {"start": v(137.79, -41.78) * mm, "end": v(138.21, -41.08) * mm});
            skLineSegment(sketch, "E402", {"start": v(138.21, -41.08) * mm, "end": v(138.94, -41.47) * mm});
            skLineSegment(sketch, "E403", {"start": v(138.94, -41.47) * mm, "end": v(138.94, -41.47) * mm});
            skLineSegment(sketch, "E404", {"start": v(139.7, -41.8) * mm, "end": v(139.42, -42.56) * mm});
            skLineSegment(sketch, "E405", {"start": v(139.51, -44.29) * mm, "end": v(139.66, -44.75) * mm});
            skLineSegment(sketch, "E406", {"start": v(140.55, -44.95) * mm, "end": v(140.88, -44.6) * mm});
            skLineSegment(sketch, "E407", {"start": v(141.16, -44.23) * mm, "end": v(141.4, -43.86) * mm});
            skLineSegment(sketch, "E408", {"start": v(141.8, -42.27) * mm, "end": v(142.62, -42.31) * mm});
            skLineSegment(sketch, "E409", {"start": v(142.62, -42.31) * mm, "end": v(142.62, -42.31) * mm});
            skLineSegment(sketch, "E410", {"start": v(142.62, -42.31) * mm, "end": v(143.44, -42.27) * mm});
            skLineSegment(sketch, "E411", {"start": v(143.44, -42.27) * mm, "end": v(143.52, -43.09) * mm});
            skLineSegment(sketch, "E412", {"start": v(143.52, -43.09) * mm, "end": v(143.64, -43.48) * mm});
            skLineSegment(sketch, "E413", {"start": v(143.64, -43.48) * mm, "end": v(143.83, -43.86) * mm});
            skLineSegment(sketch, "E414", {"start": v(143.83, -43.86) * mm, "end": v(144.07, -44.23) * mm});
            skLineSegment(sketch, "E415", {"start": v(144.07, -44.23) * mm, "end": v(144.36, -44.6) * mm});
            skLineSegment(sketch, "E416", {"start": v(144.36, -44.6) * mm, "end": v(144.69, -44.95) * mm});
            skLineSegment(sketch, "E417", {"start": v(144.69, -44.95) * mm, "end": v(145.58, -44.75) * mm});
            skLineSegment(sketch, "E418", {"start": v(145.58, -44.75) * mm, "end": v(145.72, -44.29) * mm});
            skLineSegment(sketch, "E419", {"start": v(145.72, -44.29) * mm, "end": v(145.82, -43.84) * mm});
            skLineSegment(sketch, "E420", {"start": v(145.82, -43.84) * mm, "end": v(145.88, -43.4) * mm});
            skLineSegment(sketch, "E421", {"start": v(145.88, -43.4) * mm, "end": v(145.88, -42.97) * mm});
            skLineSegment(sketch, "E422", {"start": v(145.88, -42.97) * mm, "end": v(145.82, -42.56) * mm});
            skLineSegment(sketch, "E423", {"start": v(145.82, -42.56) * mm, "end": v(145.54, -41.8) * mm});
            skLineSegment(sketch, "E424", {"start": v(145.54, -41.8) * mm, "end": v(146.3, -41.47) * mm});
            skLineSegment(sketch, "E425", {"start": v(146.3, -41.47) * mm, "end": v(146.3, -41.47) * mm});
            skLineSegment(sketch, "E426", {"start": v(146.3, -41.47) * mm, "end": v(147.03, -41.08) * mm});
            skLineSegment(sketch, "E427", {"start": v(147.03, -41.08) * mm, "end": v(147.45, -41.78) * mm});
            skLineSegment(sketch, "E428", {"start": v(147.45, -41.78) * mm, "end": v(147.73, -42.08) * mm});
            skLineSegment(sketch, "E429", {"start": v(147.73, -42.08) * mm, "end": v(148.07, -42.34) * mm});
            skLineSegment(sketch, "E430", {"start": v(148.07, -42.34) * mm, "end": v(148.45, -42.57) * mm});
            skLineSegment(sketch, "E431", {"start": v(148.45, -42.57) * mm, "end": v(148.86, -42.78) * mm});
            skLineSegment(sketch, "E432", {"start": v(148.86, -42.78) * mm, "end": v(149.3, -42.95) * mm});
            skLineSegment(sketch, "E433", {"start": v(149.3, -42.95) * mm, "end": v(150.02, -42.38) * mm});
            skLineSegment(sketch, "E434", {"start": v(150.02, -42.38) * mm, "end": v(149.95, -41.9) * mm});
            skLineSegment(sketch, "E435", {"start": v(149.95, -41.9) * mm, "end": v(149.85, -41.45) * mm});
            skLineSegment(sketch, "E436", {"start": v(149.85, -41.45) * mm, "end": v(149.7, -41.03) * mm});
            skLineSegment(sketch, "E437", {"start": v(149.7, -41.03) * mm, "end": v(149.53, -40.64) * mm});
            skLineSegment(sketch, "E438", {"start": v(149.53, -40.64) * mm, "end": v(149.3, -40.3) * mm});
            skLineSegment(sketch, "E439", {"start": v(149.3, -40.3) * mm, "end": v(148.7, -39.74) * mm});
            skLineSegment(sketch, "E440", {"start": v(148.7, -39.74) * mm, "end": v(149.25, -39.12) * mm});
            skLineSegment(sketch, "E441", {"start": v(149.25, -39.12) * mm, "end": v(149.25, -39.12) * mm});
            skLineSegment(sketch, "E442", {"start": v(149.25, -39.12) * mm, "end": v(149.73, -38.45) * mm});
            skLineSegment(sketch, "E443", {"start": v(149.73, -38.45) * mm, "end": v(150.42, -38.9) * mm});
            skLineSegment(sketch, "E444", {"start": v(150.42, -38.9) * mm, "end": v(150.8, -39.04) * mm});
            skLineSegment(sketch, "E445", {"start": v(150.8, -39.04) * mm, "end": v(151.22, -39.13) * mm});
            skLineSegment(sketch, "E446", {"start": v(151.22, -39.13) * mm, "end": v(151.66, -39.18) * mm});
            skLineSegment(sketch, "E447", {"start": v(151.66, -39.18) * mm, "end": v(152.13, -39.18) * mm});
            skLineSegment(sketch, "E448", {"start": v(152.13, -39.18) * mm, "end": v(152.6, -39.14) * mm});
            skLineSegment(sketch, "E449", {"start": v(152.6, -39.14) * mm, "end": v(153, -38.32) * mm});
            skLineSegment(sketch, "E450", {"start": v(153, -38.32) * mm, "end": v(152.73, -37.92) * mm});
            skLineSegment(sketch, "E451", {"start": v(152.73, -37.92) * mm, "end": v(152.44, -37.56) * mm});
            skLineSegment(sketch, "E452", {"start": v(152.44, -37.56) * mm, "end": v(152.13, -37.24) * mm});
            skLineSegment(sketch, "E453", {"start": v(152.13, -37.24) * mm, "end": v(151.8, -36.97) * mm});
            skLineSegment(sketch, "E454", {"start": v(151.8, -36.97) * mm, "end": v(151.44, -36.77) * mm});
            skLineSegment(sketch, "E455", {"start": v(151.44, -36.77) * mm, "end": v(150.67, -36.5) * mm});
            skLineSegment(sketch, "E456", {"start": v(150.67, -36.5) * mm, "end": v(150.9, -35.71) * mm});
            skLineSegment(sketch, "E457", {"start": v(150.9, -35.71) * mm, "end": v(150.9, -35.72) * mm});
            skLineSegment(sketch, "E458", {"start": v(134.62, -28.68) * mm, "end": v(134.62, -13.9) * mm});
            skLineSegment(sketch, "E459", {"start": v(132.62, 26.17) * mm, "end": v(132.62, 41.17) * mm});
            skLineSegment(sketch, "E460", {"start": v(132.62, 41.17) * mm, "end": v(135.55, 41.17) * mm});
            skLineSegment(sketch, "E461", {"start": v(152.62, -34.89) * mm, "end": v(152.62, 24.1) * mm});
            skArc(sketch, "E462", {"start": v(152.62, 24.1) * mm, "mid": v(152.24, 26.02) * mm, "end": v(151.15, 27.64) * mm});
            skLineSegment(sketch, "E463", {"start": v(139.08, 39.7) * mm, "end": v(151.15, 27.64) * mm});
            skArc(sketch, "E464", {"start": v(139.08, 39.7) * mm, "mid": v(137.46, 40.8) * mm, "end": v(135.55, 41.17) * mm});
            skLineSegment(sketch, "E465", {"start": v(132.62, 26.17) * mm, "end": v(141.15, 17.64) * mm});
            skArc(sketch, "E466", {"start": v(142.62, 14.1) * mm, "mid": v(142.24, 16.02) * mm, "end": v(141.15, 17.64) * mm});
            skLineSegment(sketch, "E467", {"start": v(142.62, 14.1) * mm, "end": v(142.62, -1.76) * mm});
            skArc(sketch, "E468", {"start": v(141.15, -5.3) * mm, "mid": v(142.24, -3.67) * mm, "end": v(142.62, -1.76) * mm});
            skLineSegment(sketch, "E469", {"start": v(141.15, -5.3) * mm, "end": v(136.08, -10.36) * mm});
            skArc(sketch, "E470", {"start": v(136.08, -10.36) * mm, "mid": v(135, -11.98) * mm, "end": v(134.62, -13.9) * mm});
            skLineSegment(sketch, "E471", {"start": v(134.62, -28.68) * mm, "end": v(134.44, -28.6) * mm});
            skLineSegment(sketch, "E472", {"start": v(134.44, -28.6) * mm, "end": v(134.02, -28.52) * mm});
            skLineSegment(sketch, "E473", {"start": v(134.02, -28.52) * mm, "end": v(133.57, -28.48) * mm});
            skLineSegment(sketch, "E474", {"start": v(133.57, -28.48) * mm, "end": v(133.11, -28.47) * mm});
            skLineSegment(sketch, "E475", {"start": v(133.11, -28.47) * mm, "end": v(132.63, -28.51) * mm});
            skLineSegment(sketch, "E476", {"start": v(132.63, -28.51) * mm, "end": v(132.24, -29.33) * mm});
            skLineSegment(sketch, "E477", {"start": v(132.24, -29.33) * mm, "end": v(132.5, -29.73) * mm});
            skLineSegment(sketch, "E478", {"start": v(132.5, -29.73) * mm, "end": v(132.8, -30.1) * mm});
            skLineSegment(sketch, "E479", {"start": v(132.8, -30.1) * mm, "end": v(133.1, -30.41) * mm});
            skLineSegment(sketch, "E480", {"start": v(133.1, -30.41) * mm, "end": v(133.44, -30.68) * mm});
            skLineSegment(sketch, "E481", {"start": v(133.44, -30.68) * mm, "end": v(133.8, -30.89) * mm});
            skLineSegment(sketch, "E482", {"start": v(133.8, -30.89) * mm, "end": v(134.57, -31.14) * mm});
            skLineSegment(sketch, "E483", {"start": v(134.57, -31.14) * mm, "end": v(134.35, -31.94) * mm});
            skLineSegment(sketch, "E484", {"start": v(134.35, -31.94) * mm, "end": v(134.35, -31.94) * mm});
            skLineSegment(sketch, "E485", {"start": v(134.35, -31.94) * mm, "end": v(134.2, -32.75) * mm});
            skLineSegment(sketch, "E486", {"start": v(134.2, -32.75) * mm, "end": v(133.4, -32.65) * mm});
            skLineSegment(sketch, "E487", {"start": v(133.4, -32.65) * mm, "end": v(132.98, -32.68) * mm});
            skLineSegment(sketch, "E488", {"start": v(132.98, -32.68) * mm, "end": v(132.57, -32.78) * mm});
            skLineSegment(sketch, "E489", {"start": v(132.57, -32.78) * mm, "end": v(132.15, -32.93) * mm});
            skLineSegment(sketch, "E490", {"start": v(132.15, -32.93) * mm, "end": v(131.73, -33.13) * mm});
            skLineSegment(sketch, "E491", {"start": v(131.73, -33.13) * mm, "end": v(131.31, -33.37) * mm});
            skLineSegment(sketch, "E492", {"start": v(131.31, -34.28) * mm, "end": v(131.73, -34.52) * mm});
            skLineSegment(sketch, "E493", {"start": v(131.73, -34.52) * mm, "end": v(132.15, -34.72) * mm});
            skLineSegment(sketch, "E494", {"start": v(132.15, -34.72) * mm, "end": v(132.57, -34.88) * mm});
            skLineSegment(sketch, "E495", {"start": v(132.57, -34.88) * mm, "end": v(132.98, -34.98) * mm});
            skLineSegment(sketch, "E496", {"start": v(133.4, -35) * mm, "end": v(134.2, -34.9) * mm});
            skLineSegment(sketch, "E497", {"start": v(134.35, -35.72) * mm, "end": v(134.35, -35.71) * mm});
            skLineSegment(sketch, "E498", {"start": v(134.35, -35.71) * mm, "end": v(134.57, -36.5) * mm});
            skLineSegment(sketch, "E499", {"start": v(134.57, -36.5) * mm, "end": v(133.8, -36.77) * mm});
            skLineSegment(sketch, "E500", {"start": v(133.44, -36.97) * mm, "end": v(133.1, -37.24) * mm});
            skLineSegment(sketch, "E501", {"start": v(133.1, -37.24) * mm, "end": v(132.8, -37.56) * mm});
            skLineSegment(sketch, "E502", {"start": v(132.5, -37.92) * mm, "end": v(132.24, -38.32) * mm});
            skLineSegment(sketch, "E503", {"start": v(132.24, -38.32) * mm, "end": v(132.63, -39.14) * mm});
            skLineSegment(sketch, "E504", {"start": v(132.63, -39.14) * mm, "end": v(133.11, -39.18) * mm});
            skLineSegment(sketch, "E505", {"start": v(133.11, -39.18) * mm, "end": v(133.57, -39.18) * mm});
            skLineSegment(sketch, "E506", {"start": v(135.98, -39.12) * mm, "end": v(136.53, -39.74) * mm});
            skLineSegment(sketch, "E507", {"start": v(135.94, -40.3) * mm, "end": v(135.71, -40.64) * mm});
            skLineSegment(sketch, "E508", {"start": v(135.71, -40.64) * mm, "end": v(135.53, -41.03) * mm});
            skLineSegment(sketch, "E509", {"start": v(135.53, -41.03) * mm, "end": v(135.39, -41.45) * mm});
            skLineSegment(sketch, "E510", {"start": v(135.39, -41.45) * mm, "end": v(135.28, -41.9) * mm});
            skLineSegment(sketch, "E511", {"start": v(136.37, -42.78) * mm, "end": v(136.8, -42.57) * mm});
            skLineSegment(sketch, "E512", {"start": v(137.5, -42.08) * mm, "end": v(137.79, -41.78) * mm});
            skLineSegment(sketch, "E513", {"start": v(138.94, -41.47) * mm, "end": v(139.7, -41.8) * mm});
            skLineSegment(sketch, "E514", {"start": v(139.42, -42.56) * mm, "end": v(139.35, -42.97) * mm});
            skLineSegment(sketch, "E515", {"start": v(139.35, -42.97) * mm, "end": v(139.36, -43.4) * mm});
            skLineSegment(sketch, "E516", {"start": v(139.36, -43.4) * mm, "end": v(139.41, -43.84) * mm});
            skLineSegment(sketch, "E517", {"start": v(139.41, -43.84) * mm, "end": v(139.51, -44.29) * mm});
            skLineSegment(sketch, "E518", {"start": v(139.66, -44.75) * mm, "end": v(140.55, -44.95) * mm});
            skLineSegment(sketch, "E519", {"start": v(140.88, -44.6) * mm, "end": v(141.16, -44.23) * mm});
            skLineSegment(sketch, "E520", {"start": v(141.4, -43.86) * mm, "end": v(141.6, -43.48) * mm});
            skLineSegment(sketch, "E521", {"start": v(141.6, -43.48) * mm, "end": v(141.71, -43.09) * mm});
            skLineSegment(sketch, "E522", {"start": v(141.71, -43.09) * mm, "end": v(141.8, -42.27) * mm});
            skLineSegment(sketch, "E523", {"start": v(131.31, -33.37) * mm, "end": v(131.31, -34.28) * mm});
            skCircle(sketch, "E524", {"center": v(142.62, -33.83) * mm, "radius": 0.75 * mm});
            skCircle(sketch, "E525", {"center": v(98.97, -34.17) * mm, "radius": 2.22 * mm});
            skCircle(sketch, "E526", {"center": v(98.97, -26.05) * mm, "radius": 0.55 * mm});
            skPoint(sketch, "E527.endSnap0", {"position": v(-2, -18.52) * mm});
            skLineSegment(sketch, "E528", {"start": v(-2, -15.8) * mm, "end": v(-0.05, -15.8) * mm});
            skLineSegment(sketch, "E529", {"start": v(27.56, -15.7) * mm, "end": v(27.56, -5.9) * mm});
            skLineSegment(sketch, "E530", {"start": v(-0.05, -15.8) * mm, "end": v(-0.05, -6) * mm});
            skLineSegment(sketch, "E531.trimOffspring", {"start": v(27.56, -15.7) * mm, "end": v(29.5, -15.7) * mm});
            skPoint(sketch, "E532.orphan", {"position": v(-2, -10.02) * mm});
            skLineSegment(sketch, "E533", {"start": v(-0.05, 23) * mm, "end": v(-0.05, 30) * mm});
            skLineSegment(sketch, "E534", {"start": v(27.56, 23.1) * mm, "end": v(27.56, 30.1) * mm});
            skArc(sketch, "E535", {"start": v(47.5, 10.1) * mm, "mid": v(41.67, 24.23) * mm, "end": v(27.56, 30.1) * mm});
            skPoint(sketch, "E536.endSnap0", {"position": v(-0.05, 10) * mm});
            skLineSegment(sketch, "E537", {"start": v(-20, 10) * mm, "end": v(-20, -33.15) * mm});
            skArc(sketch, "E538.trimOffspring", {"start": v(-0.05, 30) * mm, "mid": v(-14.16, 24.12) * mm, "end": v(-20, 10) * mm});
            skArc(sketch, "E539.trimOffspring", {"start": v(35.52, 2.57) * mm, "mid": v(38.42, 11.48) * mm, "end": v(33.4, 19.4) * mm});
            skLineSegment(sketch, "E540", {"start": v(27.56, -5.9) * mm, "end": v(35.52, 2.57) * mm});
            skLineSegment(sketch, "E541", {"start": v(27.56, 23.1) * mm, "end": v(33.4, 19.4) * mm});
            skArc(sketch, "E542", {"start": v(37.03, 0.54) * mm, "mid": v(40.93, 11.55) * mm, "end": v(34.79, 21.48) * mm});
            skLineSegment(sketch, "E543.MirrorCS", {"start": v(-0.05, -9) * mm, "end": v(-9.52, 0.43) * mm});
            skLineSegment(sketch, "E544", {"start": v(27.56, 26.1) * mm, "end": v(34.79, 21.48) * mm});
            skLineSegment(sketch, "E545", {"start": v(37.03, 0.54) * mm, "end": v(27.56, -9) * mm});
            skLineSegment(sketch, "E546", {"start": v(-0.05, -6) * mm, "end": v(-0.05, 23) * mm});
            skLineSegment(sketch, "E547", {"start": v(27.56, 23.1) * mm, "end": v(27.56, -9) * mm});
            skLineSegment(sketch, "E548", {"start": v(-129.43, -31.07) * mm, "end": v(-129.43, -28.07) * mm});
            skLineSegment(sketch, "E549", {"start": v(-129.43, 0.93) * mm, "end": v(-129.43, 3.93) * mm});
            skArc(sketch, "E550", {"start": v(-92.35, -21.53) * mm, "mid": v(-88.45, -10.52) * mm, "end": v(-94.6, -0.6) * mm});
            skLineSegment(sketch, "E551.MirrorCS", {"start": v(-129.43, -31.07) * mm, "end": v(-138.9, -21.63) * mm});
            skLineSegment(sketch, "E552", {"start": v(-101.82, 4.04) * mm, "end": v(-94.6, -0.6) * mm});
            skArc(sketch, "E553.trimOffspring", {"start": v(-136.66, -0.7) * mm, "mid": v(-142.8, -10.63) * mm, "end": v(-138.9, -21.63) * mm});
            skLineSegment(sketch, "E554.MirrorCS", {"start": v(-129.43, 3.93) * mm, "end": v(-136.66, -0.7) * mm});
            skLineSegment(sketch, "E555", {"start": v(-92.35, -21.53) * mm, "end": v(-101.82, -31.06) * mm});
            skLineSegment(sketch, "E556", {"start": v(-129.43, -28.07) * mm, "end": v(-129.43, 0.93) * mm});
            skLineSegment(sketch, "E557", {"start": v(-101.82, 1.04) * mm, "end": v(-101.82, -31.06) * mm});
            skLineSegment(sketch, "E558", {"start": v(-101.82, 4.04) * mm, "end": v(-101.82, 1.04) * mm});
            skLineSegment(sketch, "E559", {"start": v(-20, 0) * mm, "end": v(-12.1, 15.98) * mm});
            skLineSegment(sketch, "E560", {"start": v(47.5, 10.1) * mm, "end": v(39.85, 15.58) * mm});
            skLineSegment(sketch, "E561", {"start": v(-10, -19.95) * mm, "end": v(-10, -29.95) * mm});
            skLineSegment(sketch, "E562.0", {"start": v(0.68, -5.31) * mm, "end": v(-7.28, 3.15) * mm});
            skArc(sketch, "E562.1", {"start": v(-5.36, 18.44) * mm, "mid": v(-9.92, 11.25) * mm, "end": v(-7.28, 3.15) * mm});
            skLineSegment(sketch, "E562.2", {"start": v(0.49, 22.16) * mm, "end": v(-5.36, 18.44) * mm});
            skLineSegment(sketch, "E563.0", {"start": v(26.83, -5.2) * mm, "end": v(34.8, 3.26) * mm});
            skArc(sketch, "E563.1", {"start": v(34.8, 3.26) * mm, "mid": v(37.43, 11.35) * mm, "end": v(32.87, 18.55) * mm});
            skLineSegment(sketch, "E563.2", {"start": v(27.02, 22.26) * mm, "end": v(32.87, 18.55) * mm});
            skLineSegment(sketch, "E564.0", {"start": v(0.66, -8.3) * mm, "end": v(-8.82, 1.14) * mm});
            skArc(sketch, "E564.1", {"start": v(-6.74, 20.53) * mm, "mid": v(-12.43, 11.33) * mm, "end": v(-8.82, 1.14) * mm});
            skLineSegment(sketch, "E564.2", {"start": v(0.49, 25.16) * mm, "end": v(-6.74, 20.53) * mm});
            skLineSegment(sketch, "E565", {"start": v(-12.1, 15.98) * mm, "end": v(-10.12, 17.33) * mm});
            skLineSegment(sketch, "E566", {"start": v(-0.05, 21.82) * mm, "end": v(-6.74, 20.53) * mm});
            skLineSegment(sketch, "E567", {"start": v(-0.05, -4.54) * mm, "end": v(-7, -0.68) * mm});
            skLineSegment(sketch, "E568", {"start": v(-12.5, 10) * mm, "end": v(-27.5, 10) * mm});
            skLineSegment(sketch, "E569", {"start": v(-27.5, 10) * mm, "end": v(-27.5, 20.53) * mm});
            skLineSegment(sketch, "E570", {"start": v(-27.5, 20.53) * mm, "end": v(-6.74, 20.53) * mm});
            skLineSegment(sketch, "E571", {"start": v(-27.5, 10) * mm, "end": v(-27.5, -0.68) * mm});
            skLineSegment(sketch, "E572", {"start": v(-27.5, -0.68) * mm, "end": v(-7, -0.68) * mm});
            skLineSegment(sketch, "E573", {"start": v(-27.5, 20.53) * mm, "end": v(-27.5, 21.13) * mm});
            skLineSegment(sketch, "E574", {"start": v(-27.5, 21.13) * mm, "end": v(-5.8, 21.13) * mm});
            skLineSegment(sketch, "E575", {"start": v(-27.5, -0.68) * mm, "end": v(-27.5, -1.28) * mm});
            skLineSegment(sketch, "E576", {"start": v(-27.5, -1.28) * mm, "end": v(-6.4, -1.28) * mm});
            skSolve(sketch);
        }
        {
            var Q0;
            Q0=makeQuery(id+"F0.imprint","IMPRINT",FACE,{"disambiguationData":[TD([[makeQuery(id+"F0.imprint","IMPRINT",EDGE,{"derivedFrom":sQuery(id+"F0.wireOp",EDGE,"E0")}),1.0]])]});
            var Q1;
            Q1=makeQuery(id+"F0.imprint","IMPRINT",FACE,{"disambiguationData":[TD([[makeQuery(id+"F0.imprint","IMPRINT",EDGE,{"derivedFrom":sQuery(id+"F0.wireOp",EDGE,"E117")}),1.0]])]});
            var Q2;
            {var subQ5=sQuery(id+"F0.wireOp",EDGE,"E543.MirrorCS");Q2=makeQuery(id+"F0.imprint","IMPRINT",FACE,{"disambiguationData":[TD([[makeQuery(id+"F0.imprint","IMPRINT",EDGE,{"derivedFrom":subQ5}),-1.0]])]});}
            var Q3;
            {var subQ7=sQuery(id+"F0.wireOp",EDGE,"E559");var subQ8=sQuery(id+"F0.wireOp",EDGE,"E537");var subQ9=makeQuery(id+"F0.imprint","INTERSECT",VERTEX,{"derivedFrom":[subQ8,subQ7]});Q3=makeQuery(id+"F0.imprint","IMPRINT",FACE,{"disambiguationData":[TD([[makeQuery(id+"F0.imprint","IMPRINT",EDGE,{"disambiguationData":[TD([[subQ9,-1.0]])],"derivedFrom":subQ8}),1.0]])]});}
            var Q4;
            {var subQ0=sQuery(id+"F0.wireOp",EDGE,"E565");Q4=makeQuery(id+"F0.imprint","IMPRINT",FACE,{"disambiguationData":[TD([[makeQuery(id+"F0.imprint","IMPRINT",EDGE,{"derivedFrom":subQ0}),-1.0]])]});}
            var Q5;
            {var subQ0=sQuery(id+"F0.wireOp",EDGE,"E576");var subQ1=sQuery(id+"F0.wireOp",EDGE,"E537");var subQ2=makeQuery(id+"F0.imprint","INTERSECT",VERTEX,{"derivedFrom":[subQ1,subQ0]});Q5=makeQuery(id+"F0.imprint","IMPRINT",FACE,{"disambiguationData":[TD([[makeQuery(id+"F0.imprint","IMPRINT",EDGE,{"disambiguationData":[TD([[subQ2,1.0]])],"derivedFrom":subQ1}),1.0]])]});}
            extrude(context, id + "F1", {"entities" : qUnion([Q0, Q1, Q2, Q3, Q4, Q5]), "endBound" : BoundingType.SYMMETRIC, "depth" : 3 * mm, "offsetDistance" : 25 * mm});
        }
        {
            var Q0;
            {var subQ12=sQuery(id+"F0.wireOp",EDGE,"E562.1");Q0=makeQuery(id+"F0.imprint","IMPRINT",FACE,{"disambiguationData":[TD([[makeQuery(id+"F0.imprint","IMPRINT",EDGE,{"derivedFrom":subQ12}),-1.0]])]});}
            var Q1;
            Q1=makeQuery(id+"F0.imprint","IMPRINT",FACE,{"disambiguationData":[TD([[makeQuery(id+"F0.imprint","IMPRINT",EDGE,{"derivedFrom":sQuery(id+"F0.wireOp",EDGE,"E539.trimOffspring")}),1.0]])]});
            var Q2;
            Q2=makeQuery(id+"F0.imprint","IMPRINT",FACE,{"disambiguationData":[TD([[makeQuery(id+"F0.imprint","IMPRINT",EDGE,{"derivedFrom":sQuery(id+"F0.wireOp",EDGE,"E539.trimOffspring")}),-1.0]])]});
            var Q3;
            {var subQ5=sQuery(id+"F0.wireOp",EDGE,"E566");Q3=makeQuery(id+"F0.imprint","IMPRINT",FACE,{"disambiguationData":[TD([[makeQuery(id+"F0.imprint","IMPRINT",EDGE,{"derivedFrom":subQ5}),-1.0]])]});}
            var Q4;
            {var subQ5=sQuery(id+"F0.wireOp",EDGE,"E567");Q4=makeQuery(id+"F0.imprint","IMPRINT",FACE,{"disambiguationData":[TD([[makeQuery(id+"F0.imprint","IMPRINT",EDGE,{"derivedFrom":subQ5}),1.0]])]});}
            var Q5;
            {var subQ5=sQuery(id+"F0.wireOp",EDGE,"E562.1");Q5=makeQuery(id+"F0.imprint","IMPRINT",FACE,{"disambiguationData":[TD([[makeQuery(id+"F0.imprint","IMPRINT",EDGE,{"derivedFrom":subQ5}),1.0]])]});}
            var Q6;
            {var subQ5=sQuery(id+"F0.wireOp",EDGE,"E563.1");Q6=makeQuery(id+"F0.imprint","IMPRINT",FACE,{"disambiguationData":[TD([[makeQuery(id+"F0.imprint","IMPRINT",EDGE,{"derivedFrom":subQ5}),1.0]])]});}
            var Q7;
            {var subQ0=sQuery(id+"F0.wireOp",EDGE,"E565");Q7=makeQuery(id+"F0.imprint","IMPRINT",FACE,{"disambiguationData":[TD([[makeQuery(id+"F0.imprint","IMPRINT",EDGE,{"derivedFrom":subQ0}),1.0]])]});}
            var Q8;
            {var subQ5=sQuery(id+"F0.wireOp",EDGE,"E569");Q8=makeQuery(id+"F0.imprint","IMPRINT",FACE,{"disambiguationData":[TD([[makeQuery(id+"F0.imprint","IMPRINT",EDGE,{"derivedFrom":subQ5}),-1.0]])]});}
            var Q9;
            {var subQ3=sQuery(id+"F0.wireOp",EDGE,"E571");Q9=makeQuery(id+"F0.imprint","IMPRINT",FACE,{"disambiguationData":[TD([[makeQuery(id+"F0.imprint","IMPRINT",EDGE,{"derivedFrom":subQ3}),1.0]])]});}
            var Q10;
            {var subQ1=sQuery(id+"F0.wireOp",EDGE,"E537");var subQ3=sQuery(id+"F0.wireOp",EDGE,"E559");var subQ4=makeQuery(id+"F0.imprint","INTERSECT",VERTEX,{"derivedFrom":[subQ1,subQ3]});Q10=makeQuery(id+"F0.imprint","IMPRINT",FACE,{"disambiguationData":[TD([[makeQuery(id+"F0.imprint","IMPRINT",EDGE,{"disambiguationData":[TD([[subQ4,-1.0]])],"derivedFrom":subQ3}),1.0]])]});}
            var Q11;
            {var subQ7=sQuery(id+"F0.wireOp",EDGE,"E559");var subQ8=sQuery(id+"F0.wireOp",EDGE,"E537");var subQ9=makeQuery(id+"F0.imprint","INTERSECT",VERTEX,{"derivedFrom":[subQ8,subQ7]});Q11=makeQuery(id+"F0.imprint","IMPRINT",FACE,{"disambiguationData":[TD([[makeQuery(id+"F0.imprint","IMPRINT",EDGE,{"disambiguationData":[TD([[subQ9,-1.0]])],"derivedFrom":subQ8}),1.0]])]});}
            var Q12;
            {var subQ0=sQuery(id+"F0.wireOp",EDGE,"E565");Q12=makeQuery(id+"F0.imprint","IMPRINT",FACE,{"disambiguationData":[TD([[makeQuery(id+"F0.imprint","IMPRINT",EDGE,{"derivedFrom":subQ0}),-1.0]])]});}
            var Q13;
            {var subQ0=sQuery(id+"F0.wireOp",EDGE,"E574");var subQ1=sQuery(id+"F0.wireOp",EDGE,"E538.trimOffspring");var subQ2=makeQuery(id+"F0.imprint","INTERSECT",VERTEX,{"derivedFrom":[subQ1,subQ0]});Q13=makeQuery(id+"F0.imprint","IMPRINT",FACE,{"disambiguationData":[TD([[makeQuery(id+"F0.imprint","IMPRINT",EDGE,{"disambiguationData":[TD([[subQ2,-1.0]])],"derivedFrom":subQ1}),1.0]])]});}
            var Q14;
            {var subQ5=sQuery(id+"F0.wireOp",EDGE,"E573");Q14=makeQuery(id+"F0.imprint","IMPRINT",FACE,{"disambiguationData":[TD([[makeQuery(id+"F0.imprint","IMPRINT",EDGE,{"derivedFrom":subQ5}),-1.0]])]});}
            var Q15;
            {var subQ0=sQuery(id+"F0.wireOp",EDGE,"E572");var subQ1=sQuery(id+"F0.wireOp",EDGE,"E543.MirrorCS");var subQ2=makeQuery(id+"F0.imprint","INTERSECT",VERTEX,{"derivedFrom":[subQ1,subQ0]});Q15=makeQuery(id+"F0.imprint","IMPRINT",FACE,{"disambiguationData":[TD([[makeQuery(id+"F0.imprint","IMPRINT",EDGE,{"disambiguationData":[TD([[subQ2,1.0]])],"derivedFrom":subQ1}),-1.0]])]});}
            var Q16;
            {var subQ0=sQuery(id+"F0.wireOp",EDGE,"E576");var subQ1=sQuery(id+"F0.wireOp",EDGE,"E537");var subQ2=makeQuery(id+"F0.imprint","INTERSECT",VERTEX,{"derivedFrom":[subQ1,subQ0]});Q16=makeQuery(id+"F0.imprint","IMPRINT",FACE,{"disambiguationData":[TD([[makeQuery(id+"F0.imprint","IMPRINT",EDGE,{"disambiguationData":[TD([[subQ2,1.0]])],"derivedFrom":subQ1}),1.0]])]});}
            var Q17;
            {var subQ5=sQuery(id+"F0.wireOp",EDGE,"E575");Q17=makeQuery(id+"F0.imprint","IMPRINT",FACE,{"disambiguationData":[TD([[makeQuery(id+"F0.imprint","IMPRINT",EDGE,{"derivedFrom":subQ5}),1.0]])]});}
            extrude(context, id + "F2", {"entities" : qUnion([Q0, Q1, Q2, Q3, Q4, Q5, Q6, Q7, Q8, Q9, Q10, Q11, Q12, Q13, Q14, Q15, Q16, Q17]), "depth" : 50 * mm, "offsetDistance" : 25 * mm});
        }
        {
            var Q0;
            {var subQ12=sQuery(id+"F0.wireOp",EDGE,"E562.1");Q0=makeQuery(id+"F0.imprint","IMPRINT",FACE,{"disambiguationData":[TD([[makeQuery(id+"F0.imprint","IMPRINT",EDGE,{"derivedFrom":subQ12}),-1.0]])]});}
            var Q1;
            Q1=makeQuery(id+"F0.imprint","IMPRINT",FACE,{"disambiguationData":[TD([[makeQuery(id+"F0.imprint","IMPRINT",EDGE,{"derivedFrom":sQuery(id+"F0.wireOp",EDGE,"E539.trimOffspring")}),1.0]])]});
            var Q2;
            Q2=makeQuery(id+"F0.imprint","IMPRINT",FACE,{"disambiguationData":[TD([[makeQuery(id+"F0.imprint","IMPRINT",EDGE,{"derivedFrom":sQuery(id+"F0.wireOp",EDGE,"E539.trimOffspring")}),-1.0]])]});
            var Q3;
            {var subQ5=sQuery(id+"F0.wireOp",EDGE,"E567");Q3=makeQuery(id+"F0.imprint","IMPRINT",FACE,{"disambiguationData":[TD([[makeQuery(id+"F0.imprint","IMPRINT",EDGE,{"derivedFrom":subQ5}),1.0]])]});}
            var Q4;
            {var subQ5=sQuery(id+"F0.wireOp",EDGE,"E566");Q4=makeQuery(id+"F0.imprint","IMPRINT",FACE,{"disambiguationData":[TD([[makeQuery(id+"F0.imprint","IMPRINT",EDGE,{"derivedFrom":subQ5}),-1.0]])]});}
            extrude(context, id + "F3", {"entities" : qUnion([Q0, Q1, Q2, Q3, Q4]), "operationType" : NewBodyOperationType.ADD, "oppositeDirection" : true, "depth" : 30 * mm, "offsetDistance" : 25 * mm});
        }
        {
            var Q0;
            Q0=makeQuery(id+"F1.opExtrude","CAP_FACE",FACE,{"disambiguationData":[OSD([sQuery(id+"F0.wireOp",EDGE,"E117"),sQuery(id+"F0.wireOp",EDGE,"E118"),sQuery(id+"F0.wireOp",EDGE,"E119"),sQuery(id+"F0.wireOp",EDGE,"E120"),sQuery(id+"F0.wireOp",EDGE,"E121"),sQuery(id+"F0.wireOp",EDGE,"E122"),sQuery(id+"F0.wireOp",EDGE,"E123"),sQuery(id+"F0.wireOp",EDGE,"E124"),sQuery(id+"F0.wireOp",EDGE,"E125"),sQuery(id+"F0.wireOp",EDGE,"E126"),sQuery(id+"F0.wireOp",EDGE,"E127"),sQuery(id+"F0.wireOp",EDGE,"E128"),sQuery(id+"F0.wireOp",EDGE,"E129"),sQuery(id+"F0.wireOp",EDGE,"E131"),sQuery(id+"F0.wireOp",EDGE,"E132"),sQuery(id+"F0.wireOp",EDGE,"E133"),sQuery(id+"F0.wireOp",EDGE,"E134"),sQuery(id+"F0.wireOp",EDGE,"E135"),sQuery(id+"F0.wireOp",EDGE,"E136"),sQuery(id+"F0.wireOp",EDGE,"E137"),sQuery(id+"F0.wireOp",EDGE,"E138"),sQuery(id+"F0.wireOp",EDGE,"E140"),sQuery(id+"F0.wireOp",EDGE,"E141"),sQuery(id+"F0.wireOp",EDGE,"E142"),sQuery(id+"F0.wireOp",EDGE,"E143"),sQuery(id+"F0.wireOp",EDGE,"E144"),sQuery(id+"F0.wireOp",EDGE,"E146"),sQuery(id+"F0.wireOp",EDGE,"E147"),sQuery(id+"F0.wireOp",EDGE,"E148"),sQuery(id+"F0.wireOp",EDGE,"E149"),sQuery(id+"F0.wireOp",EDGE,"E150"),sQuery(id+"F0.wireOp",EDGE,"E151"),sQuery(id+"F0.wireOp",EDGE,"E152"),sQuery(id+"F0.wireOp",EDGE,"E153"),sQuery(id+"F0.wireOp",EDGE,"E154"),sQuery(id+"F0.wireOp",EDGE,"E155"),sQuery(id+"F0.wireOp",EDGE,"E156"),sQuery(id+"F0.wireOp",EDGE,"E157"),sQuery(id+"F0.wireOp",EDGE,"E158"),sQuery(id+"F0.wireOp",EDGE,"E159"),sQuery(id+"F0.wireOp",EDGE,"E160"),sQuery(id+"F0.wireOp",EDGE,"E162"),sQuery(id+"F0.wireOp",EDGE,"E163"),sQuery(id+"F0.wireOp",EDGE,"E164"),sQuery(id+"F0.wireOp",EDGE,"E165"),sQuery(id+"F0.wireOp",EDGE,"E166"),sQuery(id+"F0.wireOp",EDGE,"E167"),sQuery(id+"F0.wireOp",EDGE,"E168"),sQuery(id+"F0.wireOp",EDGE,"E169"),sQuery(id+"F0.wireOp",EDGE,"E170"),sQuery(id+"F0.wireOp",EDGE,"E171"),sQuery(id+"F0.wireOp",EDGE,"E172"),sQuery(id+"F0.wireOp",EDGE,"E173"),sQuery(id+"F0.wireOp",EDGE,"E174"),sQuery(id+"F0.wireOp",EDGE,"E175"),sQuery(id+"F0.wireOp",EDGE,"E176"),sQuery(id+"F0.wireOp",EDGE,"E178"),sQuery(id+"F0.wireOp",EDGE,"E179"),sQuery(id+"F0.wireOp",EDGE,"E180"),sQuery(id+"F0.wireOp",EDGE,"E181"),sQuery(id+"F0.wireOp",EDGE,"E182"),sQuery(id+"F0.wireOp",EDGE,"E183"),sQuery(id+"F0.wireOp",EDGE,"E184"),sQuery(id+"F0.wireOp",EDGE,"E185"),sQuery(id+"F0.wireOp",EDGE,"E186"),sQuery(id+"F0.wireOp",EDGE,"E187"),sQuery(id+"F0.wireOp",EDGE,"E188"),sQuery(id+"F0.wireOp",EDGE,"E189"),sQuery(id+"F0.wireOp",EDGE,"E190"),sQuery(id+"F0.wireOp",EDGE,"E191"),sQuery(id+"F0.wireOp",EDGE,"E192"),sQuery(id+"F0.wireOp",EDGE,"E193"),sQuery(id+"F0.wireOp",EDGE,"E194"),sQuery(id+"F0.wireOp",EDGE,"E195"),sQuery(id+"F0.wireOp",EDGE,"E196"),sQuery(id+"F0.wireOp",EDGE,"E197"),sQuery(id+"F0.wireOp",EDGE,"E198"),sQuery(id+"F0.wireOp",EDGE,"E199"),sQuery(id+"F0.wireOp",EDGE,"E200"),sQuery(id+"F0.wireOp",EDGE,"E201"),sQuery(id+"F0.wireOp",EDGE,"E202"),sQuery(id+"F0.wireOp",EDGE,"E203"),sQuery(id+"F0.wireOp",EDGE,"E204"),sQuery(id+"F0.wireOp",EDGE,"E205"),sQuery(id+"F0.wireOp",EDGE,"E206"),sQuery(id+"F0.wireOp",EDGE,"E207"),sQuery(id+"F0.wireOp",EDGE,"E208"),sQuery(id+"F0.wireOp",EDGE,"E210"),sQuery(id+"F0.wireOp",EDGE,"E211"),sQuery(id+"F0.wireOp",EDGE,"E212"),sQuery(id+"F0.wireOp",EDGE,"E213"),sQuery(id+"F0.wireOp",EDGE,"E214"),sQuery(id+"F0.wireOp",EDGE,"E215"),sQuery(id+"F0.wireOp",EDGE,"E216"),sQuery(id+"F0.wireOp",EDGE,"E217"),sQuery(id+"F0.wireOp",EDGE,"E218"),sQuery(id+"F0.wireOp",EDGE,"E219"),sQuery(id+"F0.wireOp",EDGE,"E220"),sQuery(id+"F0.wireOp",EDGE,"E221"),sQuery(id+"F0.wireOp",EDGE,"E223"),sQuery(id+"F0.wireOp",EDGE,"E224"),sQuery(id+"F0.wireOp",EDGE,"E225"),sQuery(id+"F0.wireOp",EDGE,"E226"),sQuery(id+"F0.wireOp",EDGE,"E227"),sQuery(id+"F0.wireOp",EDGE,"E228"),sQuery(id+"F0.wireOp",EDGE,"E229"),sQuery(id+"F0.wireOp",EDGE,"E230"),sQuery(id+"F0.wireOp",EDGE,"E231"),sQuery(id+"F0.wireOp",EDGE,"E232"),sQuery(id+"F0.wireOp",EDGE,"E233"),sQuery(id+"F0.wireOp",EDGE,"E234"),sQuery(id+"F0.wireOp",EDGE,"E235"),sQuery(id+"F0.wireOp",EDGE,"E236"),sQuery(id+"F0.wireOp",EDGE,"E237"),sQuery(id+"F0.wireOp",EDGE,"E238"),sQuery(id+"F0.wireOp",EDGE,"E239"),sQuery(id+"F0.wireOp",EDGE,"E240"),sQuery(id+"F0.wireOp",EDGE,"E241"),sQuery(id+"F0.wireOp",EDGE,"E242"),sQuery(id+"F0.wireOp",EDGE,"E243"),sQuery(id+"F0.wireOp",EDGE,"E244"),sQuery(id+"F0.wireOp",EDGE,"E245"),sQuery(id+"F0.wireOp",EDGE,"E246"),sQuery(id+"F0.wireOp",EDGE,"E247"),sQuery(id+"F0.wireOp",EDGE,"E248"),sQuery(id+"F0.wireOp",EDGE,"E249"),sQuery(id+"F0.wireOp",EDGE,"E529"),sQuery(id+"F0.wireOp",EDGE,"E531.trimOffspring"),sQuery(id+"F0.wireOp",EDGE,"E542"),sQuery(id+"F0.wireOp",EDGE,"E545"),sQuery(id+"F0.wireOp",EDGE,"E560")])],"isStart":false});
            cPlane(context, id + "F4", {"entities" : qUnion([Q0]), "cplaneType" : CPlaneType.OFFSET, "offset" : 15 * mm, "width" : 150 * mm, "height" : 150 * mm});
        }
        {
            var Q0;
            Q0=qCreatedBy(id+"F4.planeOp",FACE);
            var sketch = newSketch(context, id + "F5", { "sketchPlane" : qUnion([Q0])});
            skPoint(sketch, "E577", {"position": v(36.57, 0) * mm});
            skLineSegment(sketch, "E578", {"start": v(36.57, 0) * mm, "end": v(36.57, 18.66) * mm});
            skLineSegment(sketch, "E579", {"start": v(36.57, 18.66) * mm, "end": v(36.57, 20.2) * mm});
            skSolve(sketch);
        }
    });
